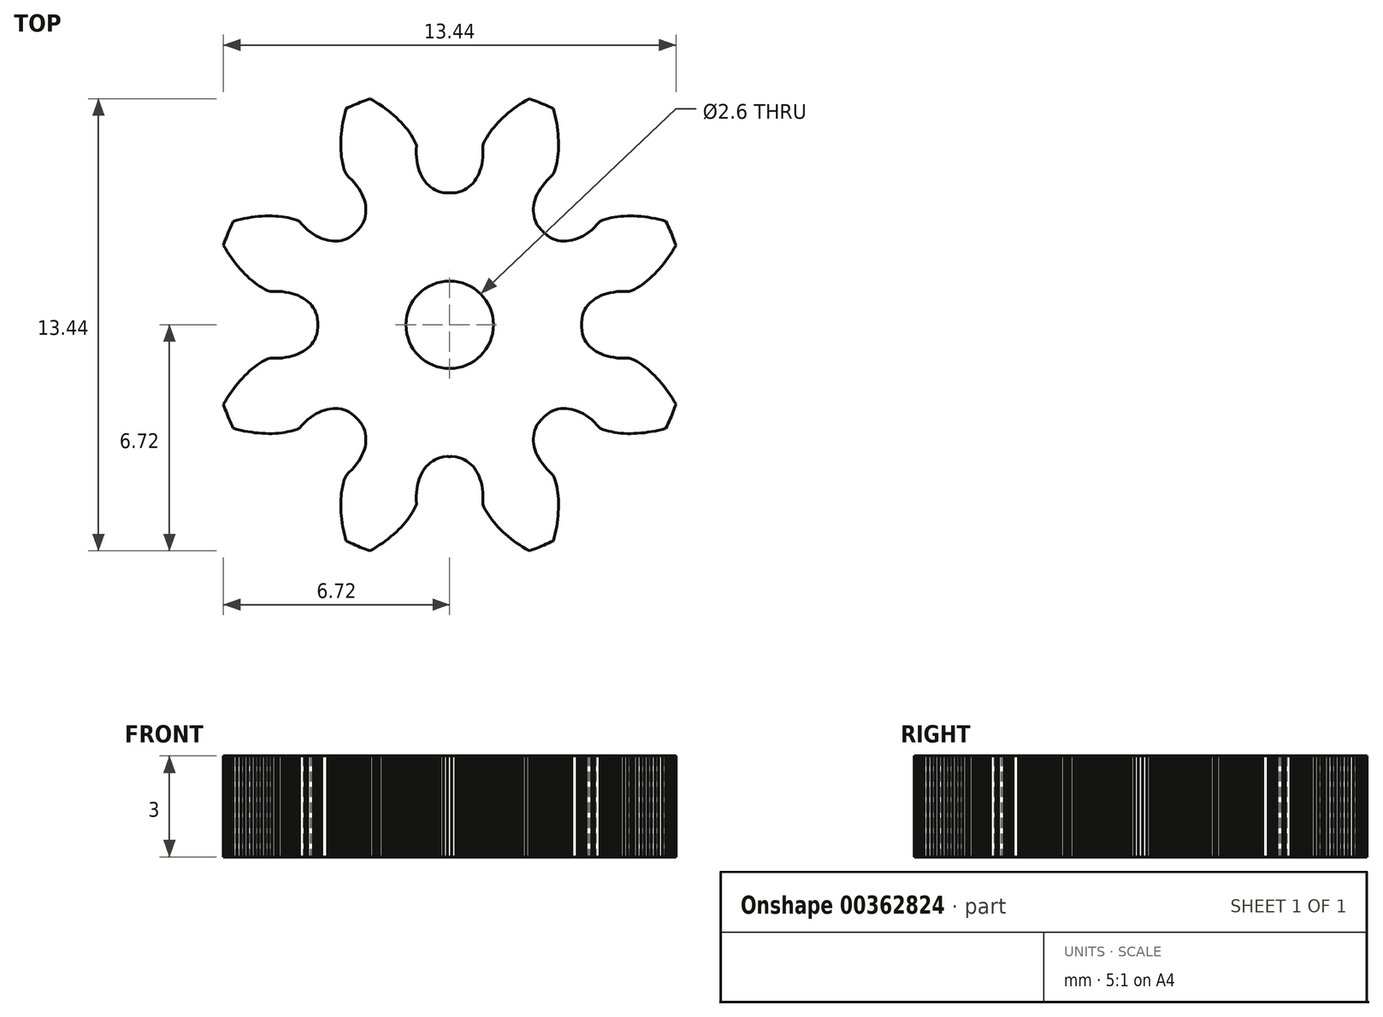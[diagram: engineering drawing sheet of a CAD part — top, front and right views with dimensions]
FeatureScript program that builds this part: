
annotation { "Feature Type Name" : "Feature", "Feature Type Description" : "" }
export const myFeature = defineFeature(function(context is Context, id is Id, definition is map)
    precondition{}
    {
        {
            var Q0;
            Q0=qCreatedBy(makeId("Top.planeOp"),FACE);
            var sketch = newSketch(context, id + "F0", { "sketchPlane" : qUnion([Q0])});
            skLineSegment(sketch, "E0", {"start": v(3.92, 0) * mm, "end": v(3.92, 0.01) * mm});
            skLineSegment(sketch, "E1", {"start": v(3.92, 0.01) * mm, "end": v(3.92, 0.03) * mm});
            skLineSegment(sketch, "E2", {"start": v(3.92, 0.03) * mm, "end": v(3.92, 0.04) * mm});
            skLineSegment(sketch, "E3", {"start": v(3.92, 0.04) * mm, "end": v(3.92, 0.05) * mm});
            skLineSegment(sketch, "E4", {"start": v(3.92, 0.05) * mm, "end": v(3.92, 0.06) * mm});
            skLineSegment(sketch, "E5", {"start": v(3.92, 0.06) * mm, "end": v(3.93, 0.18) * mm});
            skLineSegment(sketch, "E6", {"start": v(3.93, 0.18) * mm, "end": v(3.95, 0.28) * mm});
            skLineSegment(sketch, "E7", {"start": v(3.95, 0.28) * mm, "end": v(3.97, 0.36) * mm});
            skLineSegment(sketch, "E8", {"start": v(3.97, 0.36) * mm, "end": v(4, 0.44) * mm});
            skLineSegment(sketch, "E9", {"start": v(4, 0.44) * mm, "end": v(4.05, 0.5) * mm});
            skLineSegment(sketch, "E10", {"start": v(4.05, 0.5) * mm, "end": v(4.1, 0.57) * mm});
            skLineSegment(sketch, "E11", {"start": v(4.1, 0.57) * mm, "end": v(4.15, 0.63) * mm});
            skLineSegment(sketch, "E12", {"start": v(4.15, 0.63) * mm, "end": v(4.2, 0.69) * mm});
            skLineSegment(sketch, "E13", {"start": v(4.2, 0.69) * mm, "end": v(4.27, 0.74) * mm});
            skLineSegment(sketch, "E14", {"start": v(4.27, 0.74) * mm, "end": v(4.34, 0.79) * mm});
            skLineSegment(sketch, "E15", {"start": v(4.34, 0.79) * mm, "end": v(4.42, 0.83) * mm});
            skLineSegment(sketch, "E16", {"start": v(4.42, 0.83) * mm, "end": v(4.5, 0.87) * mm});
            skLineSegment(sketch, "E17", {"start": v(4.5, 0.87) * mm, "end": v(4.58, 0.9) * mm});
            skLineSegment(sketch, "E18", {"start": v(4.58, 0.9) * mm, "end": v(4.67, 0.93) * mm});
            skLineSegment(sketch, "E19", {"start": v(4.67, 0.93) * mm, "end": v(4.77, 0.96) * mm});
            skLineSegment(sketch, "E20", {"start": v(4.77, 0.96) * mm, "end": v(4.87, 0.97) * mm});
            skLineSegment(sketch, "E21", {"start": v(4.87, 0.97) * mm, "end": v(4.98, 0.99) * mm});
            skLineSegment(sketch, "E22", {"start": v(4.98, 0.99) * mm, "end": v(5.1, 1) * mm});
            skLineSegment(sketch, "E23", {"start": v(5.1, 1) * mm, "end": v(5.2, 0.99) * mm});
            skLineSegment(sketch, "E24", {"start": v(5.2, 0.99) * mm, "end": v(5.33, 0.99) * mm});
            skLineSegment(sketch, "E25", {"start": v(5.33, 0.99) * mm, "end": v(5.41, 1.02) * mm});
            skLineSegment(sketch, "E26", {"start": v(5.41, 1.02) * mm, "end": v(5.49, 1.06) * mm});
            skLineSegment(sketch, "E27", {"start": v(5.49, 1.06) * mm, "end": v(5.57, 1.1) * mm});
            skLineSegment(sketch, "E28", {"start": v(5.57, 1.1) * mm, "end": v(5.65, 1.15) * mm});
            skLineSegment(sketch, "E29", {"start": v(5.65, 1.15) * mm, "end": v(5.72, 1.2) * mm});
            skLineSegment(sketch, "E30", {"start": v(5.72, 1.2) * mm, "end": v(5.8, 1.25) * mm});
            skLineSegment(sketch, "E31", {"start": v(5.8, 1.25) * mm, "end": v(5.87, 1.31) * mm});
            skLineSegment(sketch, "E32", {"start": v(5.87, 1.31) * mm, "end": v(5.94, 1.38) * mm});
            skLineSegment(sketch, "E33", {"start": v(5.94, 1.38) * mm, "end": v(6.02, 1.44) * mm});
            skLineSegment(sketch, "E34", {"start": v(6.02, 1.44) * mm, "end": v(6.09, 1.51) * mm});
            skLineSegment(sketch, "E35", {"start": v(6.09, 1.51) * mm, "end": v(6.16, 1.58) * mm});
            skLineSegment(sketch, "E36", {"start": v(6.16, 1.58) * mm, "end": v(6.23, 1.66) * mm});
            skLineSegment(sketch, "E37", {"start": v(6.23, 1.66) * mm, "end": v(6.3, 1.74) * mm});
            skLineSegment(sketch, "E38", {"start": v(6.3, 1.74) * mm, "end": v(6.36, 1.82) * mm});
            skLineSegment(sketch, "E39", {"start": v(6.36, 1.82) * mm, "end": v(6.42, 1.9) * mm});
            skLineSegment(sketch, "E40", {"start": v(6.42, 1.9) * mm, "end": v(6.48, 2) * mm});
            skLineSegment(sketch, "E41", {"start": v(6.48, 2) * mm, "end": v(6.55, 2.08) * mm});
            skLineSegment(sketch, "E42", {"start": v(6.55, 2.08) * mm, "end": v(6.6, 2.17) * mm});
            skLineSegment(sketch, "E43", {"start": v(6.6, 2.17) * mm, "end": v(6.66, 2.27) * mm});
            skLineSegment(sketch, "E44", {"start": v(6.66, 2.27) * mm, "end": v(6.72, 2.37) * mm});
            skLineSegment(sketch, "E45", {"start": v(6.72, 2.37) * mm, "end": v(6.7, 2.44) * mm});
            skLineSegment(sketch, "E46", {"start": v(6.7, 2.44) * mm, "end": v(6.67, 2.51) * mm});
            skLineSegment(sketch, "E47", {"start": v(6.67, 2.51) * mm, "end": v(6.64, 2.58) * mm});
            skLineSegment(sketch, "E48", {"start": v(6.64, 2.58) * mm, "end": v(6.61, 2.66) * mm});
            skLineSegment(sketch, "E49", {"start": v(6.61, 2.66) * mm, "end": v(6.58, 2.73) * mm});
            skPoint(sketch, "E50", {"position": v(0, 5.7) * mm});
            skPoint(sketch, "E51", {"position": v(5.7, 0) * mm});
            skPoint(sketch, "E52", {"position": v(0, 0) * mm});
            skPoint(sketch, "E53", {"position": v(0, -5.7) * mm});
            skCircle(sketch, "E54", {"center": v(0, 0) * mm, "radius": 5.7 * mm, "construction": true});
            skLineSegment(sketch, "E55", {"start": v(5.7, 0) * mm, "end": v(-5.7, 0) * mm, "construction": true});
            skLineSegment(sketch, "E56", {"start": v(0, 5.7) * mm, "end": v(0, -5.7) * mm, "construction": true});
            skLineSegment(sketch, "E57.MirrorCS", {"start": v(3.92, 0) * mm, "end": v(3.92, -0.01) * mm});
            skLineSegment(sketch, "E58.MirrorCS", {"start": v(3.92, -0.03) * mm, "end": v(3.92, -0.04) * mm});
            skLineSegment(sketch, "E59.MirrorCS", {"start": v(3.92, -0.05) * mm, "end": v(3.92, -0.06) * mm});
            skLineSegment(sketch, "E60.MirrorCS", {"start": v(3.92, -0.01) * mm, "end": v(3.92, -0.03) * mm});
            skLineSegment(sketch, "E61.MirrorCS", {"start": v(3.92, -0.04) * mm, "end": v(3.92, -0.05) * mm});
            skLineSegment(sketch, "E62.MirrorCS", {"start": v(6.09, -1.51) * mm, "end": v(6.16, -1.58) * mm});
            skLineSegment(sketch, "E63.MirrorCS", {"start": v(4.67, -0.93) * mm, "end": v(4.77, -0.96) * mm});
            skLineSegment(sketch, "E64.MirrorCS", {"start": v(4.2, -0.69) * mm, "end": v(4.27, -0.74) * mm});
            skLineSegment(sketch, "E65.MirrorCS", {"start": v(4.27, -0.74) * mm, "end": v(4.34, -0.79) * mm});
            skLineSegment(sketch, "E66.MirrorCS", {"start": v(4.34, -0.79) * mm, "end": v(4.42, -0.83) * mm});
            skLineSegment(sketch, "E67.MirrorCS", {"start": v(3.92, -0.06) * mm, "end": v(3.93, -0.18) * mm});
            skLineSegment(sketch, "E68.MirrorCS", {"start": v(3.93, -0.18) * mm, "end": v(3.95, -0.28) * mm});
            skLineSegment(sketch, "E69.MirrorCS", {"start": v(3.95, -0.28) * mm, "end": v(3.97, -0.36) * mm});
            skLineSegment(sketch, "E70.MirrorCS", {"start": v(6.02, -1.44) * mm, "end": v(6.09, -1.51) * mm});
            skLineSegment(sketch, "E71.MirrorCS", {"start": v(3.97, -0.36) * mm, "end": v(4, -0.44) * mm});
            skLineSegment(sketch, "E72.MirrorCS", {"start": v(4, -0.44) * mm, "end": v(4.05, -0.5) * mm});
            skLineSegment(sketch, "E73.MirrorCS", {"start": v(4.05, -0.5) * mm, "end": v(4.1, -0.57) * mm});
            skLineSegment(sketch, "E74.MirrorCS", {"start": v(4.1, -0.57) * mm, "end": v(4.15, -0.63) * mm});
            skLineSegment(sketch, "E75.MirrorCS", {"start": v(4.15, -0.63) * mm, "end": v(4.2, -0.69) * mm});
            skLineSegment(sketch, "E76.MirrorCS", {"start": v(5.49, -1.06) * mm, "end": v(5.57, -1.1) * mm});
            skLineSegment(sketch, "E77.MirrorCS", {"start": v(6.6, -2.17) * mm, "end": v(6.66, -2.27) * mm});
            skLineSegment(sketch, "E78.MirrorCS", {"start": v(6.36, -1.82) * mm, "end": v(6.42, -1.9) * mm});
            skLineSegment(sketch, "E79.MirrorCS", {"start": v(5.1, -1) * mm, "end": v(5.2, -0.99) * mm});
            skLineSegment(sketch, "E80.MirrorCS", {"start": v(4.77, -0.96) * mm, "end": v(4.87, -0.97) * mm});
            skLineSegment(sketch, "E81.MirrorCS", {"start": v(6.72, -2.37) * mm, "end": v(6.7, -2.44) * mm});
            skLineSegment(sketch, "E82.MirrorCS", {"start": v(5.41, -1.02) * mm, "end": v(5.49, -1.06) * mm});
            skLineSegment(sketch, "E83.MirrorCS", {"start": v(5.65, -1.15) * mm, "end": v(5.72, -1.2) * mm});
            skLineSegment(sketch, "E84.MirrorCS", {"start": v(6.16, -1.58) * mm, "end": v(6.23, -1.66) * mm});
            skLineSegment(sketch, "E85.MirrorCS", {"start": v(4.42, -0.83) * mm, "end": v(4.5, -0.87) * mm});
            skLineSegment(sketch, "E86.MirrorCS", {"start": v(6.55, -2.08) * mm, "end": v(6.6, -2.17) * mm});
            skLineSegment(sketch, "E87.MirrorCS", {"start": v(6.64, -2.58) * mm, "end": v(6.61, -2.66) * mm});
            skLineSegment(sketch, "E88.MirrorCS", {"start": v(5.87, -1.31) * mm, "end": v(5.94, -1.38) * mm});
            skLineSegment(sketch, "E89.MirrorCS", {"start": v(6.66, -2.27) * mm, "end": v(6.72, -2.37) * mm});
            skLineSegment(sketch, "E90.MirrorCS", {"start": v(5.57, -1.1) * mm, "end": v(5.65, -1.15) * mm});
            skLineSegment(sketch, "E91.MirrorCS", {"start": v(6.42, -1.9) * mm, "end": v(6.48, -2) * mm});
            skLineSegment(sketch, "E92.MirrorCS", {"start": v(5.2, -0.99) * mm, "end": v(5.33, -0.99) * mm});
            skLineSegment(sketch, "E93.MirrorCS", {"start": v(4.87, -0.97) * mm, "end": v(4.98, -0.99) * mm});
            skLineSegment(sketch, "E94.MirrorCS", {"start": v(6.7, -2.44) * mm, "end": v(6.67, -2.51) * mm});
            skLineSegment(sketch, "E95.MirrorCS", {"start": v(5.72, -1.2) * mm, "end": v(5.8, -1.25) * mm});
            skLineSegment(sketch, "E96.MirrorCS", {"start": v(4.58, -0.9) * mm, "end": v(4.67, -0.93) * mm});
            skLineSegment(sketch, "E97.MirrorCS", {"start": v(6.23, -1.66) * mm, "end": v(6.3, -1.74) * mm});
            skLineSegment(sketch, "E98.MirrorCS", {"start": v(4.5, -0.87) * mm, "end": v(4.58, -0.9) * mm});
            skLineSegment(sketch, "E99.MirrorCS", {"start": v(6.61, -2.66) * mm, "end": v(6.58, -2.73) * mm});
            skLineSegment(sketch, "E100.MirrorCS", {"start": v(5.94, -1.38) * mm, "end": v(6.02, -1.44) * mm});
            skLineSegment(sketch, "E101.MirrorCS", {"start": v(6.48, -2) * mm, "end": v(6.55, -2.08) * mm});
            skLineSegment(sketch, "E102.MirrorCS", {"start": v(5.33, -0.99) * mm, "end": v(5.41, -1.02) * mm});
            skLineSegment(sketch, "E103.MirrorCS", {"start": v(6.67, -2.51) * mm, "end": v(6.64, -2.58) * mm});
            skLineSegment(sketch, "E104.MirrorCS", {"start": v(4.98, -0.99) * mm, "end": v(5.1, -1) * mm});
            skLineSegment(sketch, "E105.MirrorCS", {"start": v(6.3, -1.74) * mm, "end": v(6.36, -1.82) * mm});
            skLineSegment(sketch, "E106.MirrorCS", {"start": v(5.8, -1.25) * mm, "end": v(5.87, -1.31) * mm});
            skPoint(sketch, "E107.1.0", {"position": v(4.03, 4.03) * mm});
            skPoint(sketch, "E107.1.1", {"position": v(4.03, 4.03) * mm});
            skLineSegment(sketch, "E107.1.2", {"start": v(4.22, 2.82) * mm, "end": v(4.3, 2.9) * mm});
            skLineSegment(sketch, "E107.1.3", {"start": v(5.58, 3.23) * mm, "end": v(5.68, 3.22) * mm});
            skLineSegment(sketch, "E107.1.4", {"start": v(5.37, 3.23) * mm, "end": v(5.47, 3.23) * mm});
            skLineSegment(sketch, "E107.1.5", {"start": v(3.16, 6.1) * mm, "end": v(3.13, 6.2) * mm});
            skLineSegment(sketch, "E107.1.6", {"start": v(3.1, 4.54) * mm, "end": v(3.14, 4.63) * mm});
            skLineSegment(sketch, "E107.1.7", {"start": v(5.78, 3.2) * mm, "end": v(5.89, 3.2) * mm});
            skLineSegment(sketch, "E107.1.8", {"start": v(2.65, 3.96) * mm, "end": v(2.7, 4.05) * mm});
            skLineSegment(sketch, "E107.1.9", {"start": v(3.06, 2.56) * mm, "end": v(3.15, 2.52) * mm});
            skLineSegment(sketch, "E107.1.10", {"start": v(4.8, 3.18) * mm, "end": v(4.9, 3.2) * mm});
            skLineSegment(sketch, "E107.1.11", {"start": v(3.23, 5.37) * mm, "end": v(3.23, 5.47) * mm});
            skLineSegment(sketch, "E107.1.12", {"start": v(3.1, 6.32) * mm, "end": v(3.08, 6.43) * mm});
            skLineSegment(sketch, "E107.1.13", {"start": v(3.46, 2.49) * mm, "end": v(3.54, 2.5) * mm});
            skLineSegment(sketch, "E107.1.14", {"start": v(3.16, 4.71) * mm, "end": v(3.18, 4.8) * mm});
            skLineSegment(sketch, "E107.1.15", {"start": v(4.05, 2.7) * mm, "end": v(4.13, 2.76) * mm});
            skLineSegment(sketch, "E107.1.16", {"start": v(3.88, 2.6) * mm, "end": v(3.96, 2.65) * mm});
            skLineSegment(sketch, "E107.1.17", {"start": v(4.54, 3.1) * mm, "end": v(4.63, 3.14) * mm});
            skLineSegment(sketch, "E107.1.18", {"start": v(3.63, 2.51) * mm, "end": v(3.71, 2.54) * mm});
            skLineSegment(sketch, "E107.1.19", {"start": v(6.32, 3.1) * mm, "end": v(6.43, 3.08) * mm});
            skLineSegment(sketch, "E107.1.20", {"start": v(3.22, 2.5) * mm, "end": v(3.3, 2.5) * mm});
            skLineSegment(sketch, "E107.1.21", {"start": v(3.23, 5.58) * mm, "end": v(3.22, 5.68) * mm});
            skLineSegment(sketch, "E107.1.22", {"start": v(3.2, 4.9) * mm, "end": v(3.21, 4.99) * mm});
            skLineSegment(sketch, "E107.1.23", {"start": v(4.71, 3.16) * mm, "end": v(4.8, 3.18) * mm});
            skLineSegment(sketch, "E107.1.24", {"start": v(3.96, 2.65) * mm, "end": v(4.05, 2.7) * mm});
            skLineSegment(sketch, "E107.1.25", {"start": v(3.13, 6.2) * mm, "end": v(3.1, 6.32) * mm});
            skLineSegment(sketch, "E107.1.26", {"start": v(4.9, 3.2) * mm, "end": v(4.99, 3.21) * mm});
            skLineSegment(sketch, "E107.1.27", {"start": v(3.14, 4.63) * mm, "end": v(3.16, 4.71) * mm});
            skLineSegment(sketch, "E107.1.28", {"start": v(2.7, 4.05) * mm, "end": v(2.76, 4.13) * mm});
            skLineSegment(sketch, "E107.1.29", {"start": v(4.3, 2.9) * mm, "end": v(4.38, 2.98) * mm});
            skLineSegment(sketch, "E107.1.30", {"start": v(5.08, 3.22) * mm, "end": v(5.18, 3.23) * mm});
            skLineSegment(sketch, "E107.1.31", {"start": v(5.68, 3.22) * mm, "end": v(5.78, 3.2) * mm});
            skLineSegment(sketch, "E107.1.32", {"start": v(3.8, 2.57) * mm, "end": v(3.88, 2.6) * mm});
            skLineSegment(sketch, "E107.1.33", {"start": v(3.15, 2.52) * mm, "end": v(3.22, 2.5) * mm});
            skLineSegment(sketch, "E107.1.34", {"start": v(3.54, 2.5) * mm, "end": v(3.63, 2.51) * mm});
            skLineSegment(sketch, "E107.1.35", {"start": v(3.23, 5.47) * mm, "end": v(3.23, 5.58) * mm});
            skLineSegment(sketch, "E107.1.36", {"start": v(3.18, 4.8) * mm, "end": v(3.2, 4.9) * mm});
            skLineSegment(sketch, "E107.1.37", {"start": v(3.3, 2.5) * mm, "end": v(3.38, 2.49) * mm});
            skLineSegment(sketch, "E107.1.38", {"start": v(3.22, 5.68) * mm, "end": v(3.2, 5.78) * mm});
            skLineSegment(sketch, "E107.1.39", {"start": v(3.21, 4.99) * mm, "end": v(3.22, 5.08) * mm});
            skLineSegment(sketch, "E107.1.40", {"start": v(4.99, 3.21) * mm, "end": v(5.08, 3.22) * mm});
            skLineSegment(sketch, "E107.1.41", {"start": v(6.55, 2.8) * mm, "end": v(6.58, 2.73) * mm});
            skLineSegment(sketch, "E107.1.42", {"start": v(2.49, 3.46) * mm, "end": v(2.5, 3.54) * mm});
            skLineSegment(sketch, "E107.1.43", {"start": v(2.5, 3.54) * mm, "end": v(2.51, 3.63) * mm});
            skLineSegment(sketch, "E107.1.44", {"start": v(2.51, 3.63) * mm, "end": v(2.54, 3.71) * mm});
            skLineSegment(sketch, "E107.1.45", {"start": v(2.65, 2.9) * mm, "end": v(2.6, 2.99) * mm});
            skLineSegment(sketch, "E107.1.46", {"start": v(2.6, 2.99) * mm, "end": v(2.56, 3.06) * mm});
            skLineSegment(sketch, "E107.1.47", {"start": v(2.56, 3.06) * mm, "end": v(2.52, 3.15) * mm});
            skLineSegment(sketch, "E107.1.48", {"start": v(2.52, 3.15) * mm, "end": v(2.5, 3.22) * mm});
            skLineSegment(sketch, "E107.1.49", {"start": v(2.5, 3.22) * mm, "end": v(2.5, 3.3) * mm});
            skLineSegment(sketch, "E107.1.50", {"start": v(2.5, 3.3) * mm, "end": v(2.49, 3.38) * mm});
            skLineSegment(sketch, "E107.1.51", {"start": v(2.49, 3.38) * mm, "end": v(2.49, 3.46) * mm});
            skLineSegment(sketch, "E107.1.52", {"start": v(5.18, 3.23) * mm, "end": v(5.27, 3.23) * mm});
            skLineSegment(sketch, "E107.1.53", {"start": v(3.2, 5.78) * mm, "end": v(3.2, 5.89) * mm});
            skLineSegment(sketch, "E107.1.54", {"start": v(5.89, 3.2) * mm, "end": v(6, 3.18) * mm});
            skLineSegment(sketch, "E107.1.55", {"start": v(3.38, 2.49) * mm, "end": v(3.46, 2.49) * mm});
            skLineSegment(sketch, "E107.1.56", {"start": v(2.54, 3.71) * mm, "end": v(2.57, 3.8) * mm});
            skLineSegment(sketch, "E107.1.57", {"start": v(5.47, 3.23) * mm, "end": v(5.58, 3.23) * mm});
            skLineSegment(sketch, "E107.1.58", {"start": v(3.22, 5.08) * mm, "end": v(3.23, 5.18) * mm});
            skLineSegment(sketch, "E107.1.59", {"start": v(3.2, 5.89) * mm, "end": v(3.18, 6) * mm});
            skLineSegment(sketch, "E107.1.60", {"start": v(2.98, 4.38) * mm, "end": v(3.07, 4.47) * mm});
            skLineSegment(sketch, "E107.1.61", {"start": v(4.38, 2.98) * mm, "end": v(4.47, 3.07) * mm});
            skLineSegment(sketch, "E107.1.62", {"start": v(4.63, 3.14) * mm, "end": v(4.71, 3.16) * mm});
            skLineSegment(sketch, "E107.1.63", {"start": v(2.57, 3.8) * mm, "end": v(2.6, 3.88) * mm});
            skLineSegment(sketch, "E107.1.64", {"start": v(3.71, 2.54) * mm, "end": v(3.8, 2.57) * mm});
            skLineSegment(sketch, "E107.1.65", {"start": v(3.23, 5.18) * mm, "end": v(3.23, 5.27) * mm});
            skLineSegment(sketch, "E107.1.66", {"start": v(6, 3.18) * mm, "end": v(6.1, 3.16) * mm});
            skLineSegment(sketch, "E107.1.67", {"start": v(3.18, 6) * mm, "end": v(3.16, 6.1) * mm});
            skLineSegment(sketch, "E107.1.68", {"start": v(3.07, 4.47) * mm, "end": v(3.1, 4.54) * mm});
            skLineSegment(sketch, "E107.1.69", {"start": v(4.13, 2.76) * mm, "end": v(4.22, 2.82) * mm});
            skLineSegment(sketch, "E107.1.70", {"start": v(6.2, 3.13) * mm, "end": v(6.32, 3.1) * mm});
            skLineSegment(sketch, "E107.1.71", {"start": v(2.6, 3.88) * mm, "end": v(2.65, 3.96) * mm});
            skLineSegment(sketch, "E107.1.72", {"start": v(6.1, 3.16) * mm, "end": v(6.2, 3.13) * mm});
            skLineSegment(sketch, "E107.1.73", {"start": v(5.27, 3.23) * mm, "end": v(5.37, 3.23) * mm});
            skLineSegment(sketch, "E107.1.74", {"start": v(3.23, 5.27) * mm, "end": v(3.23, 5.37) * mm});
            skLineSegment(sketch, "E107.1.75", {"start": v(4.47, 3.07) * mm, "end": v(4.54, 3.1) * mm});
            skLineSegment(sketch, "E107.1.76", {"start": v(2.76, 4.13) * mm, "end": v(2.82, 4.22) * mm});
            skLineSegment(sketch, "E107.1.77", {"start": v(2.82, 4.22) * mm, "end": v(2.9, 4.3) * mm});
            skLineSegment(sketch, "E107.1.78", {"start": v(2.9, 4.3) * mm, "end": v(2.98, 4.38) * mm});
            skLineSegment(sketch, "E107.1.79", {"start": v(2.8, 6.55) * mm, "end": v(2.73, 6.58) * mm});
            skLineSegment(sketch, "E107.1.80", {"start": v(6.46, 3) * mm, "end": v(6.5, 2.94) * mm});
            skLineSegment(sketch, "E107.1.81", {"start": v(6.52, 2.87) * mm, "end": v(6.55, 2.8) * mm});
            skLineSegment(sketch, "E107.1.82", {"start": v(6.5, 2.94) * mm, "end": v(6.52, 2.87) * mm});
            skLineSegment(sketch, "E107.1.83", {"start": v(3, 6.46) * mm, "end": v(2.94, 6.5) * mm});
            skLineSegment(sketch, "E107.1.84", {"start": v(6.43, 3.08) * mm, "end": v(6.46, 3) * mm});
            skLineSegment(sketch, "E107.1.85", {"start": v(3.08, 6.43) * mm, "end": v(3, 6.46) * mm});
            skLineSegment(sketch, "E107.1.86", {"start": v(2.94, 6.5) * mm, "end": v(2.87, 6.52) * mm});
            skLineSegment(sketch, "E107.1.87", {"start": v(2.9, 2.65) * mm, "end": v(2.99, 2.6) * mm});
            skLineSegment(sketch, "E107.1.88", {"start": v(2.87, 6.52) * mm, "end": v(2.8, 6.55) * mm});
            skLineSegment(sketch, "E107.1.89", {"start": v(2.99, 2.6) * mm, "end": v(3.06, 2.56) * mm});
            skLineSegment(sketch, "E107.1.90", {"start": v(2.82, 2.73) * mm, "end": v(2.9, 2.65) * mm});
            skLineSegment(sketch, "E107.1.91", {"start": v(2.79, 2.75) * mm, "end": v(2.8, 2.74) * mm});
            skLineSegment(sketch, "E107.1.92", {"start": v(2.76, 2.78) * mm, "end": v(2.75, 2.79) * mm});
            skLineSegment(sketch, "E107.1.93", {"start": v(2.73, 2.82) * mm, "end": v(2.65, 2.9) * mm});
            skLineSegment(sketch, "E107.1.94", {"start": v(2.74, 2.8) * mm, "end": v(2.73, 2.82) * mm});
            skLineSegment(sketch, "E107.1.95", {"start": v(2.74, 2.8) * mm, "end": v(2.74, 2.8) * mm});
            skLineSegment(sketch, "E107.1.96", {"start": v(2.75, 2.79) * mm, "end": v(2.74, 2.8) * mm});
            skLineSegment(sketch, "E107.1.97", {"start": v(2.77, 2.77) * mm, "end": v(2.76, 2.78) * mm});
            skLineSegment(sketch, "E107.1.98", {"start": v(2.77, 2.77) * mm, "end": v(2.78, 2.76) * mm});
            skLineSegment(sketch, "E107.1.99", {"start": v(2.78, 2.76) * mm, "end": v(2.79, 2.75) * mm});
            skLineSegment(sketch, "E107.1.100", {"start": v(2.8, 2.74) * mm, "end": v(2.8, 2.74) * mm});
            skLineSegment(sketch, "E107.1.101", {"start": v(2.8, 2.74) * mm, "end": v(2.82, 2.73) * mm});
            skLineSegment(sketch, "E107.2.2", {"start": v(0.99, 4.98) * mm, "end": v(1, 5.1) * mm});
            skLineSegment(sketch, "E107.2.3", {"start": v(1.66, 6.23) * mm, "end": v(1.74, 6.3) * mm});
            skLineSegment(sketch, "E107.2.4", {"start": v(1.51, 6.09) * mm, "end": v(1.58, 6.16) * mm});
            skLineSegment(sketch, "E107.2.5", {"start": v(-2.08, 6.55) * mm, "end": v(-2.17, 6.6) * mm});
            skLineSegment(sketch, "E107.2.6", {"start": v(-1.02, 5.41) * mm, "end": v(-1.06, 5.49) * mm});
            skLineSegment(sketch, "E107.2.7", {"start": v(1.82, 6.36) * mm, "end": v(1.9, 6.42) * mm});
            skLineSegment(sketch, "E107.2.8", {"start": v(-0.93, 4.67) * mm, "end": v(-0.96, 4.77) * mm});
            skLineSegment(sketch, "E107.2.9", {"start": v(0.36, 3.97) * mm, "end": v(0.44, 4) * mm});
            skLineSegment(sketch, "E107.2.10", {"start": v(1.15, 5.65) * mm, "end": v(1.2, 5.72) * mm});
            skLineSegment(sketch, "E107.2.11", {"start": v(-1.51, 6.09) * mm, "end": v(-1.58, 6.16) * mm});
            skLineSegment(sketch, "E107.2.12", {"start": v(-2.27, 6.66) * mm, "end": v(-2.37, 6.72) * mm});
            skLineSegment(sketch, "E107.2.13", {"start": v(0.69, 4.2) * mm, "end": v(0.74, 4.27) * mm});
            skLineSegment(sketch, "E107.2.14", {"start": v(-1.1, 5.57) * mm, "end": v(-1.15, 5.65) * mm});
            skLineSegment(sketch, "E107.2.15", {"start": v(0.96, 4.77) * mm, "end": v(0.97, 4.87) * mm});
            skLineSegment(sketch, "E107.2.16", {"start": v(0.9, 4.58) * mm, "end": v(0.93, 4.67) * mm});
            skLineSegment(sketch, "E107.2.17", {"start": v(1.02, 5.41) * mm, "end": v(1.06, 5.49) * mm});
            skLineSegment(sketch, "E107.2.18", {"start": v(0.79, 4.34) * mm, "end": v(0.83, 4.42) * mm});
            skLineSegment(sketch, "E107.2.19", {"start": v(2.27, 6.66) * mm, "end": v(2.37, 6.72) * mm});
            skLineSegment(sketch, "E107.2.20", {"start": v(0.5, 4.05) * mm, "end": v(0.57, 4.1) * mm});
            skLineSegment(sketch, "E107.2.21", {"start": v(-1.66, 6.23) * mm, "end": v(-1.74, 6.3) * mm});
            skLineSegment(sketch, "E107.2.22", {"start": v(-1.2, 5.72) * mm, "end": v(-1.25, 5.8) * mm});
            skLineSegment(sketch, "E107.2.23", {"start": v(1.1, 5.57) * mm, "end": v(1.15, 5.65) * mm});
            skLineSegment(sketch, "E107.2.24", {"start": v(0.93, 4.67) * mm, "end": v(0.96, 4.77) * mm});
            skLineSegment(sketch, "E107.2.25", {"start": v(-2.17, 6.6) * mm, "end": v(-2.27, 6.66) * mm});
            skLineSegment(sketch, "E107.2.26", {"start": v(1.2, 5.72) * mm, "end": v(1.25, 5.8) * mm});
            skLineSegment(sketch, "E107.2.27", {"start": v(-1.06, 5.49) * mm, "end": v(-1.1, 5.57) * mm});
            skLineSegment(sketch, "E107.2.28", {"start": v(-0.96, 4.77) * mm, "end": v(-0.97, 4.87) * mm});
            skLineSegment(sketch, "E107.2.29", {"start": v(1, 5.1) * mm, "end": v(0.99, 5.2) * mm});
            skLineSegment(sketch, "E107.2.30", {"start": v(1.31, 5.87) * mm, "end": v(1.38, 5.94) * mm});
            skLineSegment(sketch, "E107.2.31", {"start": v(1.74, 6.3) * mm, "end": v(1.82, 6.36) * mm});
            skLineSegment(sketch, "E107.2.32", {"start": v(0.87, 4.5) * mm, "end": v(0.9, 4.58) * mm});
            skLineSegment(sketch, "E107.2.33", {"start": v(0.44, 4) * mm, "end": v(0.5, 4.05) * mm});
            skLineSegment(sketch, "E107.2.34", {"start": v(0.74, 4.27) * mm, "end": v(0.79, 4.34) * mm});
            skLineSegment(sketch, "E107.2.35", {"start": v(-1.58, 6.16) * mm, "end": v(-1.66, 6.23) * mm});
            skLineSegment(sketch, "E107.2.36", {"start": v(-1.15, 5.65) * mm, "end": v(-1.2, 5.72) * mm});
            skLineSegment(sketch, "E107.2.37", {"start": v(0.57, 4.1) * mm, "end": v(0.63, 4.15) * mm});
            skLineSegment(sketch, "E107.2.38", {"start": v(-1.74, 6.3) * mm, "end": v(-1.82, 6.36) * mm});
            skLineSegment(sketch, "E107.2.39", {"start": v(-1.25, 5.8) * mm, "end": v(-1.31, 5.87) * mm});
            skLineSegment(sketch, "E107.2.40", {"start": v(1.25, 5.8) * mm, "end": v(1.31, 5.87) * mm});
            skLineSegment(sketch, "E107.2.41", {"start": v(2.66, 6.61) * mm, "end": v(2.73, 6.58) * mm});
            skLineSegment(sketch, "E107.2.42", {"start": v(-0.69, 4.2) * mm, "end": v(-0.74, 4.27) * mm});
            skLineSegment(sketch, "E107.2.43", {"start": v(-0.74, 4.27) * mm, "end": v(-0.79, 4.34) * mm});
            skLineSegment(sketch, "E107.2.44", {"start": v(-0.79, 4.34) * mm, "end": v(-0.83, 4.42) * mm});
            skLineSegment(sketch, "E107.2.45", {"start": v(-0.18, 3.93) * mm, "end": v(-0.28, 3.95) * mm});
            skLineSegment(sketch, "E107.2.46", {"start": v(-0.28, 3.95) * mm, "end": v(-0.36, 3.97) * mm});
            skLineSegment(sketch, "E107.2.47", {"start": v(-0.36, 3.97) * mm, "end": v(-0.44, 4) * mm});
            skLineSegment(sketch, "E107.2.48", {"start": v(-0.44, 4) * mm, "end": v(-0.5, 4.05) * mm});
            skLineSegment(sketch, "E107.2.49", {"start": v(-0.5, 4.05) * mm, "end": v(-0.57, 4.1) * mm});
            skLineSegment(sketch, "E107.2.50", {"start": v(-0.57, 4.1) * mm, "end": v(-0.63, 4.15) * mm});
            skLineSegment(sketch, "E107.2.51", {"start": v(-0.63, 4.15) * mm, "end": v(-0.69, 4.2) * mm});
            skLineSegment(sketch, "E107.2.52", {"start": v(1.38, 5.94) * mm, "end": v(1.44, 6.02) * mm});
            skLineSegment(sketch, "E107.2.53", {"start": v(-1.82, 6.36) * mm, "end": v(-1.9, 6.42) * mm});
            skLineSegment(sketch, "E107.2.54", {"start": v(1.9, 6.42) * mm, "end": v(2, 6.48) * mm});
            skLineSegment(sketch, "E107.2.55", {"start": v(0.63, 4.15) * mm, "end": v(0.69, 4.2) * mm});
            skLineSegment(sketch, "E107.2.56", {"start": v(-0.83, 4.42) * mm, "end": v(-0.87, 4.5) * mm});
            skLineSegment(sketch, "E107.2.57", {"start": v(1.58, 6.16) * mm, "end": v(1.66, 6.23) * mm});
            skLineSegment(sketch, "E107.2.58", {"start": v(-1.31, 5.87) * mm, "end": v(-1.38, 5.94) * mm});
            skLineSegment(sketch, "E107.2.59", {"start": v(-1.9, 6.42) * mm, "end": v(-2, 6.48) * mm});
            skLineSegment(sketch, "E107.2.60", {"start": v(-0.99, 5.2) * mm, "end": v(-0.99, 5.33) * mm});
            skLineSegment(sketch, "E107.2.61", {"start": v(0.99, 5.2) * mm, "end": v(0.99, 5.33) * mm});
            skLineSegment(sketch, "E107.2.62", {"start": v(1.06, 5.49) * mm, "end": v(1.1, 5.57) * mm});
            skLineSegment(sketch, "E107.2.63", {"start": v(-0.87, 4.5) * mm, "end": v(-0.9, 4.58) * mm});
            skLineSegment(sketch, "E107.2.64", {"start": v(0.83, 4.42) * mm, "end": v(0.87, 4.5) * mm});
            skLineSegment(sketch, "E107.2.65", {"start": v(-1.38, 5.94) * mm, "end": v(-1.44, 6.02) * mm});
            skLineSegment(sketch, "E107.2.66", {"start": v(2, 6.48) * mm, "end": v(2.08, 6.55) * mm});
            skLineSegment(sketch, "E107.2.67", {"start": v(-2, 6.48) * mm, "end": v(-2.08, 6.55) * mm});
            skLineSegment(sketch, "E107.2.68", {"start": v(-0.99, 5.33) * mm, "end": v(-1.02, 5.41) * mm});
            skLineSegment(sketch, "E107.2.69", {"start": v(0.97, 4.87) * mm, "end": v(0.99, 4.98) * mm});
            skLineSegment(sketch, "E107.2.70", {"start": v(2.17, 6.6) * mm, "end": v(2.27, 6.66) * mm});
            skLineSegment(sketch, "E107.2.71", {"start": v(-0.9, 4.58) * mm, "end": v(-0.93, 4.67) * mm});
            skLineSegment(sketch, "E107.2.72", {"start": v(2.08, 6.55) * mm, "end": v(2.17, 6.6) * mm});
            skLineSegment(sketch, "E107.2.73", {"start": v(1.44, 6.02) * mm, "end": v(1.51, 6.09) * mm});
            skLineSegment(sketch, "E107.2.74", {"start": v(-1.44, 6.02) * mm, "end": v(-1.51, 6.09) * mm});
            skLineSegment(sketch, "E107.2.75", {"start": v(0.99, 5.33) * mm, "end": v(1.02, 5.41) * mm});
            skLineSegment(sketch, "E107.2.76", {"start": v(-0.97, 4.87) * mm, "end": v(-0.99, 4.98) * mm});
            skLineSegment(sketch, "E107.2.77", {"start": v(-0.99, 4.98) * mm, "end": v(-1, 5.1) * mm});
            skLineSegment(sketch, "E107.2.78", {"start": v(-1, 5.1) * mm, "end": v(-0.99, 5.2) * mm});
            skLineSegment(sketch, "E107.2.79", {"start": v(-2.66, 6.61) * mm, "end": v(-2.73, 6.58) * mm});
            skLineSegment(sketch, "E107.2.80", {"start": v(2.44, 6.7) * mm, "end": v(2.51, 6.67) * mm});
            skLineSegment(sketch, "E107.2.81", {"start": v(2.58, 6.64) * mm, "end": v(2.66, 6.61) * mm});
            skLineSegment(sketch, "E107.2.82", {"start": v(2.51, 6.67) * mm, "end": v(2.58, 6.64) * mm});
            skLineSegment(sketch, "E107.2.83", {"start": v(-2.44, 6.7) * mm, "end": v(-2.51, 6.67) * mm});
            skLineSegment(sketch, "E107.2.84", {"start": v(2.37, 6.72) * mm, "end": v(2.44, 6.7) * mm});
            skLineSegment(sketch, "E107.2.85", {"start": v(-2.37, 6.72) * mm, "end": v(-2.44, 6.7) * mm});
            skLineSegment(sketch, "E107.2.86", {"start": v(-2.51, 6.67) * mm, "end": v(-2.58, 6.64) * mm});
            skLineSegment(sketch, "E107.2.87", {"start": v(0.18, 3.93) * mm, "end": v(0.28, 3.95) * mm});
            skLineSegment(sketch, "E107.2.88", {"start": v(-2.58, 6.64) * mm, "end": v(-2.66, 6.61) * mm});
            skLineSegment(sketch, "E107.2.89", {"start": v(0.28, 3.95) * mm, "end": v(0.36, 3.97) * mm});
            skLineSegment(sketch, "E107.2.90", {"start": v(0.06, 3.92) * mm, "end": v(0.18, 3.93) * mm});
            skLineSegment(sketch, "E107.2.91", {"start": v(0.03, 3.92) * mm, "end": v(0.04, 3.92) * mm});
            skLineSegment(sketch, "E107.2.92", {"start": v(-0.01, 3.92) * mm, "end": v(-0.03, 3.92) * mm});
            skLineSegment(sketch, "E107.2.93", {"start": v(-0.06, 3.92) * mm, "end": v(-0.18, 3.93) * mm});
            skLineSegment(sketch, "E107.2.94", {"start": v(-0.05, 3.92) * mm, "end": v(-0.06, 3.92) * mm});
            skLineSegment(sketch, "E107.2.95", {"start": v(-0.04, 3.92) * mm, "end": v(-0.05, 3.92) * mm});
            skLineSegment(sketch, "E107.2.96", {"start": v(-0.03, 3.92) * mm, "end": v(-0.04, 3.92) * mm});
            skLineSegment(sketch, "E107.2.97", {"start": v(0, 3.92) * mm, "end": v(-0.01, 3.92) * mm});
            skLineSegment(sketch, "E107.2.98", {"start": v(0, 3.92) * mm, "end": v(0.01, 3.92) * mm});
            skLineSegment(sketch, "E107.2.99", {"start": v(0.01, 3.92) * mm, "end": v(0.03, 3.92) * mm});
            skLineSegment(sketch, "E107.2.100", {"start": v(0.04, 3.92) * mm, "end": v(0.05, 3.92) * mm});
            skLineSegment(sketch, "E107.2.101", {"start": v(0.05, 3.92) * mm, "end": v(0.06, 3.92) * mm});
            skPoint(sketch, "E107.3.0", {"position": v(-4.03, 4.03) * mm});
            skPoint(sketch, "E107.3.1", {"position": v(-4.03, 4.03) * mm});
            skLineSegment(sketch, "E107.3.2", {"start": v(-2.82, 4.22) * mm, "end": v(-2.9, 4.3) * mm});
            skLineSegment(sketch, "E107.3.3", {"start": v(-3.23, 5.58) * mm, "end": v(-3.22, 5.68) * mm});
            skLineSegment(sketch, "E107.3.4", {"start": v(-3.23, 5.37) * mm, "end": v(-3.23, 5.47) * mm});
            skLineSegment(sketch, "E107.3.5", {"start": v(-6.1, 3.16) * mm, "end": v(-6.2, 3.13) * mm});
            skLineSegment(sketch, "E107.3.6", {"start": v(-4.54, 3.1) * mm, "end": v(-4.63, 3.14) * mm});
            skLineSegment(sketch, "E107.3.7", {"start": v(-3.2, 5.78) * mm, "end": v(-3.2, 5.89) * mm});
            skLineSegment(sketch, "E107.3.8", {"start": v(-3.96, 2.65) * mm, "end": v(-4.05, 2.7) * mm});
            skLineSegment(sketch, "E107.3.9", {"start": v(-2.56, 3.06) * mm, "end": v(-2.52, 3.15) * mm});
            skLineSegment(sketch, "E107.3.10", {"start": v(-3.18, 4.8) * mm, "end": v(-3.2, 4.9) * mm});
            skLineSegment(sketch, "E107.3.11", {"start": v(-5.37, 3.23) * mm, "end": v(-5.47, 3.23) * mm});
            skLineSegment(sketch, "E107.3.12", {"start": v(-6.32, 3.1) * mm, "end": v(-6.43, 3.08) * mm});
            skLineSegment(sketch, "E107.3.13", {"start": v(-2.49, 3.46) * mm, "end": v(-2.5, 3.54) * mm});
            skLineSegment(sketch, "E107.3.14", {"start": v(-4.71, 3.16) * mm, "end": v(-4.8, 3.18) * mm});
            skLineSegment(sketch, "E107.3.15", {"start": v(-2.7, 4.05) * mm, "end": v(-2.76, 4.13) * mm});
            skLineSegment(sketch, "E107.3.16", {"start": v(-2.6, 3.88) * mm, "end": v(-2.65, 3.96) * mm});
            skLineSegment(sketch, "E107.3.17", {"start": v(-3.1, 4.54) * mm, "end": v(-3.14, 4.63) * mm});
            skLineSegment(sketch, "E107.3.18", {"start": v(-2.51, 3.63) * mm, "end": v(-2.54, 3.71) * mm});
            skLineSegment(sketch, "E107.3.19", {"start": v(-3.1, 6.32) * mm, "end": v(-3.08, 6.43) * mm});
            skLineSegment(sketch, "E107.3.20", {"start": v(-2.5, 3.22) * mm, "end": v(-2.5, 3.3) * mm});
            skLineSegment(sketch, "E107.3.21", {"start": v(-5.58, 3.23) * mm, "end": v(-5.68, 3.22) * mm});
            skLineSegment(sketch, "E107.3.22", {"start": v(-4.9, 3.2) * mm, "end": v(-4.99, 3.21) * mm});
            skLineSegment(sketch, "E107.3.23", {"start": v(-3.16, 4.71) * mm, "end": v(-3.18, 4.8) * mm});
            skLineSegment(sketch, "E107.3.24", {"start": v(-2.65, 3.96) * mm, "end": v(-2.7, 4.05) * mm});
            skLineSegment(sketch, "E107.3.25", {"start": v(-6.2, 3.13) * mm, "end": v(-6.32, 3.1) * mm});
            skLineSegment(sketch, "E107.3.26", {"start": v(-3.2, 4.9) * mm, "end": v(-3.21, 4.99) * mm});
            skLineSegment(sketch, "E107.3.27", {"start": v(-4.63, 3.14) * mm, "end": v(-4.71, 3.16) * mm});
            skLineSegment(sketch, "E107.3.28", {"start": v(-4.05, 2.7) * mm, "end": v(-4.13, 2.76) * mm});
            skLineSegment(sketch, "E107.3.29", {"start": v(-2.9, 4.3) * mm, "end": v(-2.98, 4.38) * mm});
            skLineSegment(sketch, "E107.3.30", {"start": v(-3.22, 5.08) * mm, "end": v(-3.23, 5.18) * mm});
            skLineSegment(sketch, "E107.3.31", {"start": v(-3.22, 5.68) * mm, "end": v(-3.2, 5.78) * mm});
            skLineSegment(sketch, "E107.3.32", {"start": v(-2.57, 3.8) * mm, "end": v(-2.6, 3.88) * mm});
            skLineSegment(sketch, "E107.3.33", {"start": v(-2.52, 3.15) * mm, "end": v(-2.5, 3.22) * mm});
            skLineSegment(sketch, "E107.3.34", {"start": v(-2.5, 3.54) * mm, "end": v(-2.51, 3.63) * mm});
            skLineSegment(sketch, "E107.3.35", {"start": v(-5.47, 3.23) * mm, "end": v(-5.58, 3.23) * mm});
            skLineSegment(sketch, "E107.3.36", {"start": v(-4.8, 3.18) * mm, "end": v(-4.9, 3.2) * mm});
            skLineSegment(sketch, "E107.3.37", {"start": v(-2.5, 3.3) * mm, "end": v(-2.49, 3.38) * mm});
            skLineSegment(sketch, "E107.3.38", {"start": v(-5.68, 3.22) * mm, "end": v(-5.78, 3.2) * mm});
            skLineSegment(sketch, "E107.3.39", {"start": v(-4.99, 3.21) * mm, "end": v(-5.08, 3.22) * mm});
            skLineSegment(sketch, "E107.3.40", {"start": v(-3.21, 4.99) * mm, "end": v(-3.22, 5.08) * mm});
            skLineSegment(sketch, "E107.3.41", {"start": v(-2.8, 6.55) * mm, "end": v(-2.73, 6.58) * mm});
            skLineSegment(sketch, "E107.3.42", {"start": v(-3.46, 2.49) * mm, "end": v(-3.54, 2.5) * mm});
            skLineSegment(sketch, "E107.3.43", {"start": v(-3.54, 2.5) * mm, "end": v(-3.63, 2.51) * mm});
            skLineSegment(sketch, "E107.3.44", {"start": v(-3.63, 2.51) * mm, "end": v(-3.71, 2.54) * mm});
            skLineSegment(sketch, "E107.3.45", {"start": v(-2.9, 2.65) * mm, "end": v(-2.99, 2.6) * mm});
            skLineSegment(sketch, "E107.3.46", {"start": v(-2.99, 2.6) * mm, "end": v(-3.06, 2.56) * mm});
            skLineSegment(sketch, "E107.3.47", {"start": v(-3.06, 2.56) * mm, "end": v(-3.15, 2.52) * mm});
            skLineSegment(sketch, "E107.3.48", {"start": v(-3.15, 2.52) * mm, "end": v(-3.22, 2.5) * mm});
            skLineSegment(sketch, "E107.3.49", {"start": v(-3.22, 2.5) * mm, "end": v(-3.3, 2.5) * mm});
            skLineSegment(sketch, "E107.3.50", {"start": v(-3.3, 2.5) * mm, "end": v(-3.38, 2.49) * mm});
            skLineSegment(sketch, "E107.3.51", {"start": v(-3.38, 2.49) * mm, "end": v(-3.46, 2.49) * mm});
            skLineSegment(sketch, "E107.3.52", {"start": v(-3.23, 5.18) * mm, "end": v(-3.23, 5.27) * mm});
            skLineSegment(sketch, "E107.3.53", {"start": v(-5.78, 3.2) * mm, "end": v(-5.89, 3.2) * mm});
            skLineSegment(sketch, "E107.3.54", {"start": v(-3.2, 5.89) * mm, "end": v(-3.18, 6) * mm});
            skLineSegment(sketch, "E107.3.55", {"start": v(-2.49, 3.38) * mm, "end": v(-2.49, 3.46) * mm});
            skLineSegment(sketch, "E107.3.56", {"start": v(-3.71, 2.54) * mm, "end": v(-3.8, 2.57) * mm});
            skLineSegment(sketch, "E107.3.57", {"start": v(-3.23, 5.47) * mm, "end": v(-3.23, 5.58) * mm});
            skLineSegment(sketch, "E107.3.58", {"start": v(-5.08, 3.22) * mm, "end": v(-5.18, 3.23) * mm});
            skLineSegment(sketch, "E107.3.59", {"start": v(-5.89, 3.2) * mm, "end": v(-6, 3.18) * mm});
            skLineSegment(sketch, "E107.3.60", {"start": v(-4.38, 2.98) * mm, "end": v(-4.47, 3.07) * mm});
            skLineSegment(sketch, "E107.3.61", {"start": v(-2.98, 4.38) * mm, "end": v(-3.07, 4.47) * mm});
            skLineSegment(sketch, "E107.3.62", {"start": v(-3.14, 4.63) * mm, "end": v(-3.16, 4.71) * mm});
            skLineSegment(sketch, "E107.3.63", {"start": v(-3.8, 2.57) * mm, "end": v(-3.88, 2.6) * mm});
            skLineSegment(sketch, "E107.3.64", {"start": v(-2.54, 3.71) * mm, "end": v(-2.57, 3.8) * mm});
            skLineSegment(sketch, "E107.3.65", {"start": v(-5.18, 3.23) * mm, "end": v(-5.27, 3.23) * mm});
            skLineSegment(sketch, "E107.3.66", {"start": v(-3.18, 6) * mm, "end": v(-3.16, 6.1) * mm});
            skLineSegment(sketch, "E107.3.67", {"start": v(-6, 3.18) * mm, "end": v(-6.1, 3.16) * mm});
            skLineSegment(sketch, "E107.3.68", {"start": v(-4.47, 3.07) * mm, "end": v(-4.54, 3.1) * mm});
            skLineSegment(sketch, "E107.3.69", {"start": v(-2.76, 4.13) * mm, "end": v(-2.82, 4.22) * mm});
            skLineSegment(sketch, "E107.3.70", {"start": v(-3.13, 6.2) * mm, "end": v(-3.1, 6.32) * mm});
            skLineSegment(sketch, "E107.3.71", {"start": v(-3.88, 2.6) * mm, "end": v(-3.96, 2.65) * mm});
            skLineSegment(sketch, "E107.3.72", {"start": v(-3.16, 6.1) * mm, "end": v(-3.13, 6.2) * mm});
            skLineSegment(sketch, "E107.3.73", {"start": v(-3.23, 5.27) * mm, "end": v(-3.23, 5.37) * mm});
            skLineSegment(sketch, "E107.3.74", {"start": v(-5.27, 3.23) * mm, "end": v(-5.37, 3.23) * mm});
            skLineSegment(sketch, "E107.3.75", {"start": v(-3.07, 4.47) * mm, "end": v(-3.1, 4.54) * mm});
            skLineSegment(sketch, "E107.3.76", {"start": v(-4.13, 2.76) * mm, "end": v(-4.22, 2.82) * mm});
            skLineSegment(sketch, "E107.3.77", {"start": v(-4.22, 2.82) * mm, "end": v(-4.3, 2.9) * mm});
            skLineSegment(sketch, "E107.3.78", {"start": v(-4.3, 2.9) * mm, "end": v(-4.38, 2.98) * mm});
            skLineSegment(sketch, "E107.3.79", {"start": v(-6.55, 2.8) * mm, "end": v(-6.58, 2.73) * mm});
            skLineSegment(sketch, "E107.3.80", {"start": v(-3, 6.46) * mm, "end": v(-2.94, 6.5) * mm});
            skLineSegment(sketch, "E107.3.81", {"start": v(-2.87, 6.52) * mm, "end": v(-2.8, 6.55) * mm});
            skLineSegment(sketch, "E107.3.82", {"start": v(-2.94, 6.5) * mm, "end": v(-2.87, 6.52) * mm});
            skLineSegment(sketch, "E107.3.83", {"start": v(-6.46, 3) * mm, "end": v(-6.5, 2.94) * mm});
            skLineSegment(sketch, "E107.3.84", {"start": v(-3.08, 6.43) * mm, "end": v(-3, 6.46) * mm});
            skLineSegment(sketch, "E107.3.85", {"start": v(-6.43, 3.08) * mm, "end": v(-6.46, 3) * mm});
            skLineSegment(sketch, "E107.3.86", {"start": v(-6.5, 2.94) * mm, "end": v(-6.52, 2.87) * mm});
            skLineSegment(sketch, "E107.3.87", {"start": v(-2.65, 2.9) * mm, "end": v(-2.6, 2.99) * mm});
            skLineSegment(sketch, "E107.3.88", {"start": v(-6.52, 2.87) * mm, "end": v(-6.55, 2.8) * mm});
            skLineSegment(sketch, "E107.3.89", {"start": v(-2.6, 2.99) * mm, "end": v(-2.56, 3.06) * mm});
            skLineSegment(sketch, "E107.3.90", {"start": v(-2.73, 2.82) * mm, "end": v(-2.65, 2.9) * mm});
            skLineSegment(sketch, "E107.3.91", {"start": v(-2.75, 2.79) * mm, "end": v(-2.74, 2.8) * mm});
            skLineSegment(sketch, "E107.3.92", {"start": v(-2.78, 2.76) * mm, "end": v(-2.79, 2.75) * mm});
            skLineSegment(sketch, "E107.3.93", {"start": v(-2.82, 2.73) * mm, "end": v(-2.9, 2.65) * mm});
            skLineSegment(sketch, "E107.3.94", {"start": v(-2.8, 2.74) * mm, "end": v(-2.82, 2.73) * mm});
            skLineSegment(sketch, "E107.3.95", {"start": v(-2.8, 2.74) * mm, "end": v(-2.8, 2.74) * mm});
            skLineSegment(sketch, "E107.3.96", {"start": v(-2.79, 2.75) * mm, "end": v(-2.8, 2.74) * mm});
            skLineSegment(sketch, "E107.3.97", {"start": v(-2.77, 2.77) * mm, "end": v(-2.78, 2.76) * mm});
            skLineSegment(sketch, "E107.3.98", {"start": v(-2.77, 2.77) * mm, "end": v(-2.76, 2.78) * mm});
            skLineSegment(sketch, "E107.3.99", {"start": v(-2.76, 2.78) * mm, "end": v(-2.75, 2.79) * mm});
            skLineSegment(sketch, "E107.3.100", {"start": v(-2.74, 2.8) * mm, "end": v(-2.74, 2.8) * mm});
            skLineSegment(sketch, "E107.3.101", {"start": v(-2.74, 2.8) * mm, "end": v(-2.73, 2.82) * mm});
            skPoint(sketch, "E107.4.0", {"position": v(-5.7, 0) * mm});
            skPoint(sketch, "E107.4.1", {"position": v(-5.7, 0) * mm});
            skLineSegment(sketch, "E107.4.2", {"start": v(-4.98, 0.99) * mm, "end": v(-5.1, 1) * mm});
            skLineSegment(sketch, "E107.4.3", {"start": v(-6.23, 1.66) * mm, "end": v(-6.3, 1.74) * mm});
            skLineSegment(sketch, "E107.4.4", {"start": v(-6.09, 1.51) * mm, "end": v(-6.16, 1.58) * mm});
            skLineSegment(sketch, "E107.4.5", {"start": v(-6.55, -2.08) * mm, "end": v(-6.6, -2.17) * mm});
            skLineSegment(sketch, "E107.4.6", {"start": v(-5.41, -1.02) * mm, "end": v(-5.49, -1.06) * mm});
            skLineSegment(sketch, "E107.4.7", {"start": v(-6.36, 1.82) * mm, "end": v(-6.42, 1.9) * mm});
            skLineSegment(sketch, "E107.4.8", {"start": v(-4.67, -0.93) * mm, "end": v(-4.77, -0.96) * mm});
            skLineSegment(sketch, "E107.4.9", {"start": v(-3.97, 0.36) * mm, "end": v(-4, 0.44) * mm});
            skLineSegment(sketch, "E107.4.10", {"start": v(-5.65, 1.15) * mm, "end": v(-5.72, 1.2) * mm});
            skLineSegment(sketch, "E107.4.11", {"start": v(-6.09, -1.51) * mm, "end": v(-6.16, -1.58) * mm});
            skLineSegment(sketch, "E107.4.12", {"start": v(-6.66, -2.27) * mm, "end": v(-6.72, -2.37) * mm});
            skLineSegment(sketch, "E107.4.13", {"start": v(-4.2, 0.69) * mm, "end": v(-4.27, 0.74) * mm});
            skLineSegment(sketch, "E107.4.14", {"start": v(-5.57, -1.1) * mm, "end": v(-5.65, -1.15) * mm});
            skLineSegment(sketch, "E107.4.15", {"start": v(-4.77, 0.96) * mm, "end": v(-4.87, 0.97) * mm});
            skLineSegment(sketch, "E107.4.16", {"start": v(-4.58, 0.9) * mm, "end": v(-4.67, 0.93) * mm});
            skLineSegment(sketch, "E107.4.17", {"start": v(-5.41, 1.02) * mm, "end": v(-5.49, 1.06) * mm});
            skLineSegment(sketch, "E107.4.18", {"start": v(-4.34, 0.79) * mm, "end": v(-4.42, 0.83) * mm});
            skLineSegment(sketch, "E107.4.19", {"start": v(-6.66, 2.27) * mm, "end": v(-6.72, 2.37) * mm});
            skLineSegment(sketch, "E107.4.20", {"start": v(-4.05, 0.5) * mm, "end": v(-4.1, 0.57) * mm});
            skLineSegment(sketch, "E107.4.21", {"start": v(-6.23, -1.66) * mm, "end": v(-6.3, -1.74) * mm});
            skLineSegment(sketch, "E107.4.22", {"start": v(-5.72, -1.2) * mm, "end": v(-5.8, -1.25) * mm});
            skLineSegment(sketch, "E107.4.23", {"start": v(-5.57, 1.1) * mm, "end": v(-5.65, 1.15) * mm});
            skLineSegment(sketch, "E107.4.24", {"start": v(-4.67, 0.93) * mm, "end": v(-4.77, 0.96) * mm});
            skLineSegment(sketch, "E107.4.25", {"start": v(-6.6, -2.17) * mm, "end": v(-6.66, -2.27) * mm});
            skLineSegment(sketch, "E107.4.26", {"start": v(-5.72, 1.2) * mm, "end": v(-5.8, 1.25) * mm});
            skLineSegment(sketch, "E107.4.27", {"start": v(-5.49, -1.06) * mm, "end": v(-5.57, -1.1) * mm});
            skLineSegment(sketch, "E107.4.28", {"start": v(-4.77, -0.96) * mm, "end": v(-4.87, -0.97) * mm});
            skLineSegment(sketch, "E107.4.29", {"start": v(-5.1, 1) * mm, "end": v(-5.2, 0.99) * mm});
            skLineSegment(sketch, "E107.4.30", {"start": v(-5.87, 1.31) * mm, "end": v(-5.94, 1.38) * mm});
            skLineSegment(sketch, "E107.4.31", {"start": v(-6.3, 1.74) * mm, "end": v(-6.36, 1.82) * mm});
            skLineSegment(sketch, "E107.4.32", {"start": v(-4.5, 0.87) * mm, "end": v(-4.58, 0.9) * mm});
            skLineSegment(sketch, "E107.4.33", {"start": v(-4, 0.44) * mm, "end": v(-4.05, 0.5) * mm});
            skLineSegment(sketch, "E107.4.34", {"start": v(-4.27, 0.74) * mm, "end": v(-4.34, 0.79) * mm});
            skLineSegment(sketch, "E107.4.35", {"start": v(-6.16, -1.58) * mm, "end": v(-6.23, -1.66) * mm});
            skLineSegment(sketch, "E107.4.36", {"start": v(-5.65, -1.15) * mm, "end": v(-5.72, -1.2) * mm});
            skLineSegment(sketch, "E107.4.37", {"start": v(-4.1, 0.57) * mm, "end": v(-4.15, 0.63) * mm});
            skLineSegment(sketch, "E107.4.38", {"start": v(-6.3, -1.74) * mm, "end": v(-6.36, -1.82) * mm});
            skLineSegment(sketch, "E107.4.39", {"start": v(-5.8, -1.25) * mm, "end": v(-5.87, -1.31) * mm});
            skLineSegment(sketch, "E107.4.40", {"start": v(-5.8, 1.25) * mm, "end": v(-5.87, 1.31) * mm});
            skLineSegment(sketch, "E107.4.41", {"start": v(-6.61, 2.66) * mm, "end": v(-6.58, 2.73) * mm});
            skLineSegment(sketch, "E107.4.42", {"start": v(-4.2, -0.69) * mm, "end": v(-4.27, -0.74) * mm});
            skLineSegment(sketch, "E107.4.43", {"start": v(-4.27, -0.74) * mm, "end": v(-4.34, -0.79) * mm});
            skLineSegment(sketch, "E107.4.44", {"start": v(-4.34, -0.79) * mm, "end": v(-4.42, -0.83) * mm});
            skLineSegment(sketch, "E107.4.45", {"start": v(-3.93, -0.18) * mm, "end": v(-3.95, -0.28) * mm});
            skLineSegment(sketch, "E107.4.46", {"start": v(-3.95, -0.28) * mm, "end": v(-3.97, -0.36) * mm});
            skLineSegment(sketch, "E107.4.47", {"start": v(-3.97, -0.36) * mm, "end": v(-4, -0.44) * mm});
            skLineSegment(sketch, "E107.4.48", {"start": v(-4, -0.44) * mm, "end": v(-4.05, -0.5) * mm});
            skLineSegment(sketch, "E107.4.49", {"start": v(-4.05, -0.5) * mm, "end": v(-4.1, -0.57) * mm});
            skLineSegment(sketch, "E107.4.50", {"start": v(-4.1, -0.57) * mm, "end": v(-4.15, -0.63) * mm});
            skLineSegment(sketch, "E107.4.51", {"start": v(-4.15, -0.63) * mm, "end": v(-4.2, -0.69) * mm});
            skLineSegment(sketch, "E107.4.52", {"start": v(-5.94, 1.38) * mm, "end": v(-6.02, 1.44) * mm});
            skLineSegment(sketch, "E107.4.53", {"start": v(-6.36, -1.82) * mm, "end": v(-6.42, -1.9) * mm});
            skLineSegment(sketch, "E107.4.54", {"start": v(-6.42, 1.9) * mm, "end": v(-6.48, 2) * mm});
            skLineSegment(sketch, "E107.4.55", {"start": v(-4.15, 0.63) * mm, "end": v(-4.2, 0.69) * mm});
            skLineSegment(sketch, "E107.4.56", {"start": v(-4.42, -0.83) * mm, "end": v(-4.5, -0.87) * mm});
            skLineSegment(sketch, "E107.4.57", {"start": v(-6.16, 1.58) * mm, "end": v(-6.23, 1.66) * mm});
            skLineSegment(sketch, "E107.4.58", {"start": v(-5.87, -1.31) * mm, "end": v(-5.94, -1.38) * mm});
            skLineSegment(sketch, "E107.4.59", {"start": v(-6.42, -1.9) * mm, "end": v(-6.48, -2) * mm});
            skLineSegment(sketch, "E107.4.60", {"start": v(-5.2, -0.99) * mm, "end": v(-5.33, -0.99) * mm});
            skLineSegment(sketch, "E107.4.61", {"start": v(-5.2, 0.99) * mm, "end": v(-5.33, 0.99) * mm});
            skLineSegment(sketch, "E107.4.62", {"start": v(-5.49, 1.06) * mm, "end": v(-5.57, 1.1) * mm});
            skLineSegment(sketch, "E107.4.63", {"start": v(-4.5, -0.87) * mm, "end": v(-4.58, -0.9) * mm});
            skLineSegment(sketch, "E107.4.64", {"start": v(-4.42, 0.83) * mm, "end": v(-4.5, 0.87) * mm});
            skLineSegment(sketch, "E107.4.65", {"start": v(-5.94, -1.38) * mm, "end": v(-6.02, -1.44) * mm});
            skLineSegment(sketch, "E107.4.66", {"start": v(-6.48, 2) * mm, "end": v(-6.55, 2.08) * mm});
            skLineSegment(sketch, "E107.4.67", {"start": v(-6.48, -2) * mm, "end": v(-6.55, -2.08) * mm});
            skLineSegment(sketch, "E107.4.68", {"start": v(-5.33, -0.99) * mm, "end": v(-5.41, -1.02) * mm});
            skLineSegment(sketch, "E107.4.69", {"start": v(-4.87, 0.97) * mm, "end": v(-4.98, 0.99) * mm});
            skLineSegment(sketch, "E107.4.70", {"start": v(-6.6, 2.17) * mm, "end": v(-6.66, 2.27) * mm});
            skLineSegment(sketch, "E107.4.71", {"start": v(-4.58, -0.9) * mm, "end": v(-4.67, -0.93) * mm});
            skLineSegment(sketch, "E107.4.72", {"start": v(-6.55, 2.08) * mm, "end": v(-6.6, 2.17) * mm});
            skLineSegment(sketch, "E107.4.73", {"start": v(-6.02, 1.44) * mm, "end": v(-6.09, 1.51) * mm});
            skLineSegment(sketch, "E107.4.74", {"start": v(-6.02, -1.44) * mm, "end": v(-6.09, -1.51) * mm});
            skLineSegment(sketch, "E107.4.75", {"start": v(-5.33, 0.99) * mm, "end": v(-5.41, 1.02) * mm});
            skLineSegment(sketch, "E107.4.76", {"start": v(-4.87, -0.97) * mm, "end": v(-4.98, -0.99) * mm});
            skLineSegment(sketch, "E107.4.77", {"start": v(-4.98, -0.99) * mm, "end": v(-5.1, -1) * mm});
            skLineSegment(sketch, "E107.4.78", {"start": v(-5.1, -1) * mm, "end": v(-5.2, -0.99) * mm});
            skLineSegment(sketch, "E107.4.79", {"start": v(-6.61, -2.66) * mm, "end": v(-6.58, -2.73) * mm});
            skLineSegment(sketch, "E107.4.80", {"start": v(-6.7, 2.44) * mm, "end": v(-6.67, 2.51) * mm});
            skLineSegment(sketch, "E107.4.81", {"start": v(-6.64, 2.58) * mm, "end": v(-6.61, 2.66) * mm});
            skLineSegment(sketch, "E107.4.82", {"start": v(-6.67, 2.51) * mm, "end": v(-6.64, 2.58) * mm});
            skLineSegment(sketch, "E107.4.83", {"start": v(-6.7, -2.44) * mm, "end": v(-6.67, -2.51) * mm});
            skLineSegment(sketch, "E107.4.84", {"start": v(-6.72, 2.37) * mm, "end": v(-6.7, 2.44) * mm});
            skLineSegment(sketch, "E107.4.85", {"start": v(-6.72, -2.37) * mm, "end": v(-6.7, -2.44) * mm});
            skLineSegment(sketch, "E107.4.86", {"start": v(-6.67, -2.51) * mm, "end": v(-6.64, -2.58) * mm});
            skLineSegment(sketch, "E107.4.87", {"start": v(-3.93, 0.18) * mm, "end": v(-3.95, 0.28) * mm});
            skLineSegment(sketch, "E107.4.88", {"start": v(-6.64, -2.58) * mm, "end": v(-6.61, -2.66) * mm});
            skLineSegment(sketch, "E107.4.89", {"start": v(-3.95, 0.28) * mm, "end": v(-3.97, 0.36) * mm});
            skLineSegment(sketch, "E107.4.90", {"start": v(-3.92, 0.06) * mm, "end": v(-3.93, 0.18) * mm});
            skLineSegment(sketch, "E107.4.91", {"start": v(-3.92, 0.03) * mm, "end": v(-3.92, 0.04) * mm});
            skLineSegment(sketch, "E107.4.92", {"start": v(-3.92, -0.01) * mm, "end": v(-3.92, -0.03) * mm});
            skLineSegment(sketch, "E107.4.93", {"start": v(-3.92, -0.06) * mm, "end": v(-3.93, -0.18) * mm});
            skLineSegment(sketch, "E107.4.94", {"start": v(-3.92, -0.05) * mm, "end": v(-3.92, -0.06) * mm});
            skLineSegment(sketch, "E107.4.95", {"start": v(-3.92, -0.04) * mm, "end": v(-3.92, -0.05) * mm});
            skLineSegment(sketch, "E107.4.96", {"start": v(-3.92, -0.03) * mm, "end": v(-3.92, -0.04) * mm});
            skLineSegment(sketch, "E107.4.97", {"start": v(-3.92, 0) * mm, "end": v(-3.92, -0.01) * mm});
            skLineSegment(sketch, "E107.4.98", {"start": v(-3.92, 0) * mm, "end": v(-3.92, 0.01) * mm});
            skLineSegment(sketch, "E107.4.99", {"start": v(-3.92, 0.01) * mm, "end": v(-3.92, 0.03) * mm});
            skLineSegment(sketch, "E107.4.100", {"start": v(-3.92, 0.04) * mm, "end": v(-3.92, 0.05) * mm});
            skLineSegment(sketch, "E107.4.101", {"start": v(-3.92, 0.05) * mm, "end": v(-3.92, 0.06) * mm});
            skPoint(sketch, "E107.5.0", {"position": v(-4.03, -4.03) * mm});
            skPoint(sketch, "E107.5.1", {"position": v(-4.03, -4.03) * mm});
            skLineSegment(sketch, "E107.5.2", {"start": v(-4.22, -2.82) * mm, "end": v(-4.3, -2.9) * mm});
            skLineSegment(sketch, "E107.5.3", {"start": v(-5.58, -3.23) * mm, "end": v(-5.68, -3.22) * mm});
            skLineSegment(sketch, "E107.5.4", {"start": v(-5.37, -3.23) * mm, "end": v(-5.47, -3.23) * mm});
            skLineSegment(sketch, "E107.5.5", {"start": v(-3.16, -6.1) * mm, "end": v(-3.13, -6.2) * mm});
            skLineSegment(sketch, "E107.5.6", {"start": v(-3.1, -4.54) * mm, "end": v(-3.14, -4.63) * mm});
            skLineSegment(sketch, "E107.5.7", {"start": v(-5.78, -3.2) * mm, "end": v(-5.89, -3.2) * mm});
            skLineSegment(sketch, "E107.5.8", {"start": v(-2.65, -3.96) * mm, "end": v(-2.7, -4.05) * mm});
            skLineSegment(sketch, "E107.5.9", {"start": v(-3.06, -2.56) * mm, "end": v(-3.15, -2.52) * mm});
            skLineSegment(sketch, "E107.5.10", {"start": v(-4.8, -3.18) * mm, "end": v(-4.9, -3.2) * mm});
            skLineSegment(sketch, "E107.5.11", {"start": v(-3.23, -5.37) * mm, "end": v(-3.23, -5.47) * mm});
            skLineSegment(sketch, "E107.5.12", {"start": v(-3.1, -6.32) * mm, "end": v(-3.08, -6.43) * mm});
            skLineSegment(sketch, "E107.5.13", {"start": v(-3.46, -2.49) * mm, "end": v(-3.54, -2.5) * mm});
            skLineSegment(sketch, "E107.5.14", {"start": v(-3.16, -4.71) * mm, "end": v(-3.18, -4.8) * mm});
            skLineSegment(sketch, "E107.5.15", {"start": v(-4.05, -2.7) * mm, "end": v(-4.13, -2.76) * mm});
            skLineSegment(sketch, "E107.5.16", {"start": v(-3.88, -2.6) * mm, "end": v(-3.96, -2.65) * mm});
            skLineSegment(sketch, "E107.5.17", {"start": v(-4.54, -3.1) * mm, "end": v(-4.63, -3.14) * mm});
            skLineSegment(sketch, "E107.5.18", {"start": v(-3.63, -2.51) * mm, "end": v(-3.71, -2.54) * mm});
            skLineSegment(sketch, "E107.5.19", {"start": v(-6.32, -3.1) * mm, "end": v(-6.43, -3.08) * mm});
            skLineSegment(sketch, "E107.5.20", {"start": v(-3.22, -2.5) * mm, "end": v(-3.3, -2.5) * mm});
            skLineSegment(sketch, "E107.5.21", {"start": v(-3.23, -5.58) * mm, "end": v(-3.22, -5.68) * mm});
            skLineSegment(sketch, "E107.5.22", {"start": v(-3.2, -4.9) * mm, "end": v(-3.21, -4.99) * mm});
            skLineSegment(sketch, "E107.5.23", {"start": v(-4.71, -3.16) * mm, "end": v(-4.8, -3.18) * mm});
            skLineSegment(sketch, "E107.5.24", {"start": v(-3.96, -2.65) * mm, "end": v(-4.05, -2.7) * mm});
            skLineSegment(sketch, "E107.5.25", {"start": v(-3.13, -6.2) * mm, "end": v(-3.1, -6.32) * mm});
            skLineSegment(sketch, "E107.5.26", {"start": v(-4.9, -3.2) * mm, "end": v(-4.99, -3.21) * mm});
            skLineSegment(sketch, "E107.5.27", {"start": v(-3.14, -4.63) * mm, "end": v(-3.16, -4.71) * mm});
            skLineSegment(sketch, "E107.5.28", {"start": v(-2.7, -4.05) * mm, "end": v(-2.76, -4.13) * mm});
            skLineSegment(sketch, "E107.5.29", {"start": v(-4.3, -2.9) * mm, "end": v(-4.38, -2.98) * mm});
            skLineSegment(sketch, "E107.5.30", {"start": v(-5.08, -3.22) * mm, "end": v(-5.18, -3.23) * mm});
            skLineSegment(sketch, "E107.5.31", {"start": v(-5.68, -3.22) * mm, "end": v(-5.78, -3.2) * mm});
            skLineSegment(sketch, "E107.5.32", {"start": v(-3.8, -2.57) * mm, "end": v(-3.88, -2.6) * mm});
            skLineSegment(sketch, "E107.5.33", {"start": v(-3.15, -2.52) * mm, "end": v(-3.22, -2.5) * mm});
            skLineSegment(sketch, "E107.5.34", {"start": v(-3.54, -2.5) * mm, "end": v(-3.63, -2.51) * mm});
            skLineSegment(sketch, "E107.5.35", {"start": v(-3.23, -5.47) * mm, "end": v(-3.23, -5.58) * mm});
            skLineSegment(sketch, "E107.5.36", {"start": v(-3.18, -4.8) * mm, "end": v(-3.2, -4.9) * mm});
            skLineSegment(sketch, "E107.5.37", {"start": v(-3.3, -2.5) * mm, "end": v(-3.38, -2.49) * mm});
            skLineSegment(sketch, "E107.5.38", {"start": v(-3.22, -5.68) * mm, "end": v(-3.2, -5.78) * mm});
            skLineSegment(sketch, "E107.5.39", {"start": v(-3.21, -4.99) * mm, "end": v(-3.22, -5.08) * mm});
            skLineSegment(sketch, "E107.5.40", {"start": v(-4.99, -3.21) * mm, "end": v(-5.08, -3.22) * mm});
            skLineSegment(sketch, "E107.5.41", {"start": v(-6.55, -2.8) * mm, "end": v(-6.58, -2.73) * mm});
            skLineSegment(sketch, "E107.5.42", {"start": v(-2.49, -3.46) * mm, "end": v(-2.5, -3.54) * mm});
            skLineSegment(sketch, "E107.5.43", {"start": v(-2.5, -3.54) * mm, "end": v(-2.51, -3.63) * mm});
            skLineSegment(sketch, "E107.5.44", {"start": v(-2.51, -3.63) * mm, "end": v(-2.54, -3.71) * mm});
            skLineSegment(sketch, "E107.5.45", {"start": v(-2.65, -2.9) * mm, "end": v(-2.6, -2.99) * mm});
            skLineSegment(sketch, "E107.5.46", {"start": v(-2.6, -2.99) * mm, "end": v(-2.56, -3.06) * mm});
            skLineSegment(sketch, "E107.5.47", {"start": v(-2.56, -3.06) * mm, "end": v(-2.52, -3.15) * mm});
            skLineSegment(sketch, "E107.5.48", {"start": v(-2.52, -3.15) * mm, "end": v(-2.5, -3.22) * mm});
            skLineSegment(sketch, "E107.5.49", {"start": v(-2.5, -3.22) * mm, "end": v(-2.5, -3.3) * mm});
            skLineSegment(sketch, "E107.5.50", {"start": v(-2.5, -3.3) * mm, "end": v(-2.49, -3.38) * mm});
            skLineSegment(sketch, "E107.5.51", {"start": v(-2.49, -3.38) * mm, "end": v(-2.49, -3.46) * mm});
            skLineSegment(sketch, "E107.5.52", {"start": v(-5.18, -3.23) * mm, "end": v(-5.27, -3.23) * mm});
            skLineSegment(sketch, "E107.5.53", {"start": v(-3.2, -5.78) * mm, "end": v(-3.2, -5.89) * mm});
            skLineSegment(sketch, "E107.5.54", {"start": v(-5.89, -3.2) * mm, "end": v(-6, -3.18) * mm});
            skLineSegment(sketch, "E107.5.55", {"start": v(-3.38, -2.49) * mm, "end": v(-3.46, -2.49) * mm});
            skLineSegment(sketch, "E107.5.56", {"start": v(-2.54, -3.71) * mm, "end": v(-2.57, -3.8) * mm});
            skLineSegment(sketch, "E107.5.57", {"start": v(-5.47, -3.23) * mm, "end": v(-5.58, -3.23) * mm});
            skLineSegment(sketch, "E107.5.58", {"start": v(-3.22, -5.08) * mm, "end": v(-3.23, -5.18) * mm});
            skLineSegment(sketch, "E107.5.59", {"start": v(-3.2, -5.89) * mm, "end": v(-3.18, -6) * mm});
            skLineSegment(sketch, "E107.5.60", {"start": v(-2.98, -4.38) * mm, "end": v(-3.07, -4.47) * mm});
            skLineSegment(sketch, "E107.5.61", {"start": v(-4.38, -2.98) * mm, "end": v(-4.47, -3.07) * mm});
            skLineSegment(sketch, "E107.5.62", {"start": v(-4.63, -3.14) * mm, "end": v(-4.71, -3.16) * mm});
            skLineSegment(sketch, "E107.5.63", {"start": v(-2.57, -3.8) * mm, "end": v(-2.6, -3.88) * mm});
            skLineSegment(sketch, "E107.5.64", {"start": v(-3.71, -2.54) * mm, "end": v(-3.8, -2.57) * mm});
            skLineSegment(sketch, "E107.5.65", {"start": v(-3.23, -5.18) * mm, "end": v(-3.23, -5.27) * mm});
            skLineSegment(sketch, "E107.5.66", {"start": v(-6, -3.18) * mm, "end": v(-6.1, -3.16) * mm});
            skLineSegment(sketch, "E107.5.67", {"start": v(-3.18, -6) * mm, "end": v(-3.16, -6.1) * mm});
            skLineSegment(sketch, "E107.5.68", {"start": v(-3.07, -4.47) * mm, "end": v(-3.1, -4.54) * mm});
            skLineSegment(sketch, "E107.5.69", {"start": v(-4.13, -2.76) * mm, "end": v(-4.22, -2.82) * mm});
            skLineSegment(sketch, "E107.5.70", {"start": v(-6.2, -3.13) * mm, "end": v(-6.32, -3.1) * mm});
            skLineSegment(sketch, "E107.5.71", {"start": v(-2.6, -3.88) * mm, "end": v(-2.65, -3.96) * mm});
            skLineSegment(sketch, "E107.5.72", {"start": v(-6.1, -3.16) * mm, "end": v(-6.2, -3.13) * mm});
            skLineSegment(sketch, "E107.5.73", {"start": v(-5.27, -3.23) * mm, "end": v(-5.37, -3.23) * mm});
            skLineSegment(sketch, "E107.5.74", {"start": v(-3.23, -5.27) * mm, "end": v(-3.23, -5.37) * mm});
            skLineSegment(sketch, "E107.5.75", {"start": v(-4.47, -3.07) * mm, "end": v(-4.54, -3.1) * mm});
            skLineSegment(sketch, "E107.5.76", {"start": v(-2.76, -4.13) * mm, "end": v(-2.82, -4.22) * mm});
            skLineSegment(sketch, "E107.5.77", {"start": v(-2.82, -4.22) * mm, "end": v(-2.9, -4.3) * mm});
            skLineSegment(sketch, "E107.5.78", {"start": v(-2.9, -4.3) * mm, "end": v(-2.98, -4.38) * mm});
            skLineSegment(sketch, "E107.5.79", {"start": v(-2.8, -6.55) * mm, "end": v(-2.73, -6.58) * mm});
            skLineSegment(sketch, "E107.5.80", {"start": v(-6.46, -3) * mm, "end": v(-6.5, -2.94) * mm});
            skLineSegment(sketch, "E107.5.81", {"start": v(-6.52, -2.87) * mm, "end": v(-6.55, -2.8) * mm});
            skLineSegment(sketch, "E107.5.82", {"start": v(-6.5, -2.94) * mm, "end": v(-6.52, -2.87) * mm});
            skLineSegment(sketch, "E107.5.83", {"start": v(-3, -6.46) * mm, "end": v(-2.94, -6.5) * mm});
            skLineSegment(sketch, "E107.5.84", {"start": v(-6.43, -3.08) * mm, "end": v(-6.46, -3) * mm});
            skLineSegment(sketch, "E107.5.85", {"start": v(-3.08, -6.43) * mm, "end": v(-3, -6.46) * mm});
            skLineSegment(sketch, "E107.5.86", {"start": v(-2.94, -6.5) * mm, "end": v(-2.87, -6.52) * mm});
            skLineSegment(sketch, "E107.5.87", {"start": v(-2.9, -2.65) * mm, "end": v(-2.99, -2.6) * mm});
            skLineSegment(sketch, "E107.5.88", {"start": v(-2.87, -6.52) * mm, "end": v(-2.8, -6.55) * mm});
            skLineSegment(sketch, "E107.5.89", {"start": v(-2.99, -2.6) * mm, "end": v(-3.06, -2.56) * mm});
            skLineSegment(sketch, "E107.5.90", {"start": v(-2.82, -2.73) * mm, "end": v(-2.9, -2.65) * mm});
            skLineSegment(sketch, "E107.5.91", {"start": v(-2.79, -2.75) * mm, "end": v(-2.8, -2.74) * mm});
            skLineSegment(sketch, "E107.5.92", {"start": v(-2.76, -2.78) * mm, "end": v(-2.75, -2.79) * mm});
            skLineSegment(sketch, "E107.5.93", {"start": v(-2.73, -2.82) * mm, "end": v(-2.65, -2.9) * mm});
            skLineSegment(sketch, "E107.5.94", {"start": v(-2.74, -2.8) * mm, "end": v(-2.73, -2.82) * mm});
            skLineSegment(sketch, "E107.5.95", {"start": v(-2.74, -2.8) * mm, "end": v(-2.74, -2.8) * mm});
            skLineSegment(sketch, "E107.5.96", {"start": v(-2.75, -2.79) * mm, "end": v(-2.74, -2.8) * mm});
            skLineSegment(sketch, "E107.5.97", {"start": v(-2.77, -2.77) * mm, "end": v(-2.76, -2.78) * mm});
            skLineSegment(sketch, "E107.5.98", {"start": v(-2.77, -2.77) * mm, "end": v(-2.78, -2.76) * mm});
            skLineSegment(sketch, "E107.5.99", {"start": v(-2.78, -2.76) * mm, "end": v(-2.79, -2.75) * mm});
            skLineSegment(sketch, "E107.5.100", {"start": v(-2.8, -2.74) * mm, "end": v(-2.8, -2.74) * mm});
            skLineSegment(sketch, "E107.5.101", {"start": v(-2.8, -2.74) * mm, "end": v(-2.82, -2.73) * mm});
            skLineSegment(sketch, "E107.6.2", {"start": v(-0.99, -4.98) * mm, "end": v(-1, -5.1) * mm});
            skLineSegment(sketch, "E107.6.3", {"start": v(-1.66, -6.23) * mm, "end": v(-1.74, -6.3) * mm});
            skLineSegment(sketch, "E107.6.4", {"start": v(-1.51, -6.09) * mm, "end": v(-1.58, -6.16) * mm});
            skLineSegment(sketch, "E107.6.5", {"start": v(2.08, -6.55) * mm, "end": v(2.17, -6.6) * mm});
            skLineSegment(sketch, "E107.6.6", {"start": v(1.02, -5.41) * mm, "end": v(1.06, -5.49) * mm});
            skLineSegment(sketch, "E107.6.7", {"start": v(-1.82, -6.36) * mm, "end": v(-1.9, -6.42) * mm});
            skLineSegment(sketch, "E107.6.8", {"start": v(0.93, -4.67) * mm, "end": v(0.96, -4.77) * mm});
            skLineSegment(sketch, "E107.6.9", {"start": v(-0.36, -3.97) * mm, "end": v(-0.44, -4) * mm});
            skLineSegment(sketch, "E107.6.10", {"start": v(-1.15, -5.65) * mm, "end": v(-1.2, -5.72) * mm});
            skLineSegment(sketch, "E107.6.11", {"start": v(1.51, -6.09) * mm, "end": v(1.58, -6.16) * mm});
            skLineSegment(sketch, "E107.6.12", {"start": v(2.27, -6.66) * mm, "end": v(2.37, -6.72) * mm});
            skLineSegment(sketch, "E107.6.13", {"start": v(-0.69, -4.2) * mm, "end": v(-0.74, -4.27) * mm});
            skLineSegment(sketch, "E107.6.14", {"start": v(1.1, -5.57) * mm, "end": v(1.15, -5.65) * mm});
            skLineSegment(sketch, "E107.6.15", {"start": v(-0.96, -4.77) * mm, "end": v(-0.97, -4.87) * mm});
            skLineSegment(sketch, "E107.6.16", {"start": v(-0.9, -4.58) * mm, "end": v(-0.93, -4.67) * mm});
            skLineSegment(sketch, "E107.6.17", {"start": v(-1.02, -5.41) * mm, "end": v(-1.06, -5.49) * mm});
            skLineSegment(sketch, "E107.6.18", {"start": v(-0.79, -4.34) * mm, "end": v(-0.83, -4.42) * mm});
            skLineSegment(sketch, "E107.6.19", {"start": v(-2.27, -6.66) * mm, "end": v(-2.37, -6.72) * mm});
            skLineSegment(sketch, "E107.6.20", {"start": v(-0.5, -4.05) * mm, "end": v(-0.57, -4.1) * mm});
            skLineSegment(sketch, "E107.6.21", {"start": v(1.66, -6.23) * mm, "end": v(1.74, -6.3) * mm});
            skLineSegment(sketch, "E107.6.22", {"start": v(1.2, -5.72) * mm, "end": v(1.25, -5.8) * mm});
            skLineSegment(sketch, "E107.6.23", {"start": v(-1.1, -5.57) * mm, "end": v(-1.15, -5.65) * mm});
            skLineSegment(sketch, "E107.6.24", {"start": v(-0.93, -4.67) * mm, "end": v(-0.96, -4.77) * mm});
            skLineSegment(sketch, "E107.6.25", {"start": v(2.17, -6.6) * mm, "end": v(2.27, -6.66) * mm});
            skLineSegment(sketch, "E107.6.26", {"start": v(-1.2, -5.72) * mm, "end": v(-1.25, -5.8) * mm});
            skLineSegment(sketch, "E107.6.27", {"start": v(1.06, -5.49) * mm, "end": v(1.1, -5.57) * mm});
            skLineSegment(sketch, "E107.6.28", {"start": v(0.96, -4.77) * mm, "end": v(0.97, -4.87) * mm});
            skLineSegment(sketch, "E107.6.29", {"start": v(-1, -5.1) * mm, "end": v(-0.99, -5.2) * mm});
            skLineSegment(sketch, "E107.6.30", {"start": v(-1.31, -5.87) * mm, "end": v(-1.38, -5.94) * mm});
            skLineSegment(sketch, "E107.6.31", {"start": v(-1.74, -6.3) * mm, "end": v(-1.82, -6.36) * mm});
            skLineSegment(sketch, "E107.6.32", {"start": v(-0.87, -4.5) * mm, "end": v(-0.9, -4.58) * mm});
            skLineSegment(sketch, "E107.6.33", {"start": v(-0.44, -4) * mm, "end": v(-0.5, -4.05) * mm});
            skLineSegment(sketch, "E107.6.34", {"start": v(-0.74, -4.27) * mm, "end": v(-0.79, -4.34) * mm});
            skLineSegment(sketch, "E107.6.35", {"start": v(1.58, -6.16) * mm, "end": v(1.66, -6.23) * mm});
            skLineSegment(sketch, "E107.6.36", {"start": v(1.15, -5.65) * mm, "end": v(1.2, -5.72) * mm});
            skLineSegment(sketch, "E107.6.37", {"start": v(-0.57, -4.1) * mm, "end": v(-0.63, -4.15) * mm});
            skLineSegment(sketch, "E107.6.38", {"start": v(1.74, -6.3) * mm, "end": v(1.82, -6.36) * mm});
            skLineSegment(sketch, "E107.6.39", {"start": v(1.25, -5.8) * mm, "end": v(1.31, -5.87) * mm});
            skLineSegment(sketch, "E107.6.40", {"start": v(-1.25, -5.8) * mm, "end": v(-1.31, -5.87) * mm});
            skLineSegment(sketch, "E107.6.41", {"start": v(-2.66, -6.61) * mm, "end": v(-2.73, -6.58) * mm});
            skLineSegment(sketch, "E107.6.42", {"start": v(0.69, -4.2) * mm, "end": v(0.74, -4.27) * mm});
            skLineSegment(sketch, "E107.6.43", {"start": v(0.74, -4.27) * mm, "end": v(0.79, -4.34) * mm});
            skLineSegment(sketch, "E107.6.44", {"start": v(0.79, -4.34) * mm, "end": v(0.83, -4.42) * mm});
            skLineSegment(sketch, "E107.6.45", {"start": v(0.18, -3.93) * mm, "end": v(0.28, -3.95) * mm});
            skLineSegment(sketch, "E107.6.46", {"start": v(0.28, -3.95) * mm, "end": v(0.36, -3.97) * mm});
            skLineSegment(sketch, "E107.6.47", {"start": v(0.36, -3.97) * mm, "end": v(0.44, -4) * mm});
            skLineSegment(sketch, "E107.6.48", {"start": v(0.44, -4) * mm, "end": v(0.5, -4.05) * mm});
            skLineSegment(sketch, "E107.6.49", {"start": v(0.5, -4.05) * mm, "end": v(0.57, -4.1) * mm});
            skLineSegment(sketch, "E107.6.50", {"start": v(0.57, -4.1) * mm, "end": v(0.63, -4.15) * mm});
            skLineSegment(sketch, "E107.6.51", {"start": v(0.63, -4.15) * mm, "end": v(0.69, -4.2) * mm});
            skLineSegment(sketch, "E107.6.52", {"start": v(-1.38, -5.94) * mm, "end": v(-1.44, -6.02) * mm});
            skLineSegment(sketch, "E107.6.53", {"start": v(1.82, -6.36) * mm, "end": v(1.9, -6.42) * mm});
            skLineSegment(sketch, "E107.6.54", {"start": v(-1.9, -6.42) * mm, "end": v(-2, -6.48) * mm});
            skLineSegment(sketch, "E107.6.55", {"start": v(-0.63, -4.15) * mm, "end": v(-0.69, -4.2) * mm});
            skLineSegment(sketch, "E107.6.56", {"start": v(0.83, -4.42) * mm, "end": v(0.87, -4.5) * mm});
            skLineSegment(sketch, "E107.6.57", {"start": v(-1.58, -6.16) * mm, "end": v(-1.66, -6.23) * mm});
            skLineSegment(sketch, "E107.6.58", {"start": v(1.31, -5.87) * mm, "end": v(1.38, -5.94) * mm});
            skLineSegment(sketch, "E107.6.59", {"start": v(1.9, -6.42) * mm, "end": v(2, -6.48) * mm});
            skLineSegment(sketch, "E107.6.60", {"start": v(0.99, -5.2) * mm, "end": v(0.99, -5.33) * mm});
            skLineSegment(sketch, "E107.6.61", {"start": v(-0.99, -5.2) * mm, "end": v(-0.99, -5.33) * mm});
            skLineSegment(sketch, "E107.6.62", {"start": v(-1.06, -5.49) * mm, "end": v(-1.1, -5.57) * mm});
            skLineSegment(sketch, "E107.6.63", {"start": v(0.87, -4.5) * mm, "end": v(0.9, -4.58) * mm});
            skLineSegment(sketch, "E107.6.64", {"start": v(-0.83, -4.42) * mm, "end": v(-0.87, -4.5) * mm});
            skLineSegment(sketch, "E107.6.65", {"start": v(1.38, -5.94) * mm, "end": v(1.44, -6.02) * mm});
            skLineSegment(sketch, "E107.6.66", {"start": v(-2, -6.48) * mm, "end": v(-2.08, -6.55) * mm});
            skLineSegment(sketch, "E107.6.67", {"start": v(2, -6.48) * mm, "end": v(2.08, -6.55) * mm});
            skLineSegment(sketch, "E107.6.68", {"start": v(0.99, -5.33) * mm, "end": v(1.02, -5.41) * mm});
            skLineSegment(sketch, "E107.6.69", {"start": v(-0.97, -4.87) * mm, "end": v(-0.99, -4.98) * mm});
            skLineSegment(sketch, "E107.6.70", {"start": v(-2.17, -6.6) * mm, "end": v(-2.27, -6.66) * mm});
            skLineSegment(sketch, "E107.6.71", {"start": v(0.9, -4.58) * mm, "end": v(0.93, -4.67) * mm});
            skLineSegment(sketch, "E107.6.72", {"start": v(-2.08, -6.55) * mm, "end": v(-2.17, -6.6) * mm});
            skLineSegment(sketch, "E107.6.73", {"start": v(-1.44, -6.02) * mm, "end": v(-1.51, -6.09) * mm});
            skLineSegment(sketch, "E107.6.74", {"start": v(1.44, -6.02) * mm, "end": v(1.51, -6.09) * mm});
            skLineSegment(sketch, "E107.6.75", {"start": v(-0.99, -5.33) * mm, "end": v(-1.02, -5.41) * mm});
            skLineSegment(sketch, "E107.6.76", {"start": v(0.97, -4.87) * mm, "end": v(0.99, -4.98) * mm});
            skLineSegment(sketch, "E107.6.77", {"start": v(0.99, -4.98) * mm, "end": v(1, -5.1) * mm});
            skLineSegment(sketch, "E107.6.78", {"start": v(1, -5.1) * mm, "end": v(0.99, -5.2) * mm});
            skLineSegment(sketch, "E107.6.79", {"start": v(2.66, -6.61) * mm, "end": v(2.73, -6.58) * mm});
            skLineSegment(sketch, "E107.6.80", {"start": v(-2.44, -6.7) * mm, "end": v(-2.51, -6.67) * mm});
            skLineSegment(sketch, "E107.6.81", {"start": v(-2.58, -6.64) * mm, "end": v(-2.66, -6.61) * mm});
            skLineSegment(sketch, "E107.6.82", {"start": v(-2.51, -6.67) * mm, "end": v(-2.58, -6.64) * mm});
            skLineSegment(sketch, "E107.6.83", {"start": v(2.44, -6.7) * mm, "end": v(2.51, -6.67) * mm});
            skLineSegment(sketch, "E107.6.84", {"start": v(-2.37, -6.72) * mm, "end": v(-2.44, -6.7) * mm});
            skLineSegment(sketch, "E107.6.85", {"start": v(2.37, -6.72) * mm, "end": v(2.44, -6.7) * mm});
            skLineSegment(sketch, "E107.6.86", {"start": v(2.51, -6.67) * mm, "end": v(2.58, -6.64) * mm});
            skLineSegment(sketch, "E107.6.87", {"start": v(-0.18, -3.93) * mm, "end": v(-0.28, -3.95) * mm});
            skLineSegment(sketch, "E107.6.88", {"start": v(2.58, -6.64) * mm, "end": v(2.66, -6.61) * mm});
            skLineSegment(sketch, "E107.6.89", {"start": v(-0.28, -3.95) * mm, "end": v(-0.36, -3.97) * mm});
            skLineSegment(sketch, "E107.6.90", {"start": v(-0.06, -3.92) * mm, "end": v(-0.18, -3.93) * mm});
            skLineSegment(sketch, "E107.6.91", {"start": v(-0.03, -3.92) * mm, "end": v(-0.04, -3.92) * mm});
            skLineSegment(sketch, "E107.6.92", {"start": v(0.01, -3.92) * mm, "end": v(0.03, -3.92) * mm});
            skLineSegment(sketch, "E107.6.93", {"start": v(0.06, -3.92) * mm, "end": v(0.18, -3.93) * mm});
            skLineSegment(sketch, "E107.6.94", {"start": v(0.05, -3.92) * mm, "end": v(0.06, -3.92) * mm});
            skLineSegment(sketch, "E107.6.95", {"start": v(0.04, -3.92) * mm, "end": v(0.05, -3.92) * mm});
            skLineSegment(sketch, "E107.6.96", {"start": v(0.03, -3.92) * mm, "end": v(0.04, -3.92) * mm});
            skLineSegment(sketch, "E107.6.97", {"start": v(0, -3.92) * mm, "end": v(0.01, -3.92) * mm});
            skLineSegment(sketch, "E107.6.98", {"start": v(0, -3.92) * mm, "end": v(-0.01, -3.92) * mm});
            skLineSegment(sketch, "E107.6.99", {"start": v(-0.01, -3.92) * mm, "end": v(-0.03, -3.92) * mm});
            skLineSegment(sketch, "E107.6.100", {"start": v(-0.04, -3.92) * mm, "end": v(-0.05, -3.92) * mm});
            skLineSegment(sketch, "E107.6.101", {"start": v(-0.05, -3.92) * mm, "end": v(-0.06, -3.92) * mm});
            skPoint(sketch, "E107.7.0", {"position": v(4.03, -4.03) * mm});
            skPoint(sketch, "E107.7.1", {"position": v(4.03, -4.03) * mm});
            skLineSegment(sketch, "E107.7.2", {"start": v(2.82, -4.22) * mm, "end": v(2.9, -4.3) * mm});
            skLineSegment(sketch, "E107.7.3", {"start": v(3.23, -5.58) * mm, "end": v(3.22, -5.68) * mm});
            skLineSegment(sketch, "E107.7.4", {"start": v(3.23, -5.37) * mm, "end": v(3.23, -5.47) * mm});
            skLineSegment(sketch, "E107.7.5", {"start": v(6.1, -3.16) * mm, "end": v(6.2, -3.13) * mm});
            skLineSegment(sketch, "E107.7.6", {"start": v(4.54, -3.1) * mm, "end": v(4.63, -3.14) * mm});
            skLineSegment(sketch, "E107.7.7", {"start": v(3.2, -5.78) * mm, "end": v(3.2, -5.89) * mm});
            skLineSegment(sketch, "E107.7.8", {"start": v(3.96, -2.65) * mm, "end": v(4.05, -2.7) * mm});
            skLineSegment(sketch, "E107.7.9", {"start": v(2.56, -3.06) * mm, "end": v(2.52, -3.15) * mm});
            skLineSegment(sketch, "E107.7.10", {"start": v(3.18, -4.8) * mm, "end": v(3.2, -4.9) * mm});
            skLineSegment(sketch, "E107.7.11", {"start": v(5.37, -3.23) * mm, "end": v(5.47, -3.23) * mm});
            skLineSegment(sketch, "E107.7.12", {"start": v(6.32, -3.1) * mm, "end": v(6.43, -3.08) * mm});
            skLineSegment(sketch, "E107.7.13", {"start": v(2.49, -3.46) * mm, "end": v(2.5, -3.54) * mm});
            skLineSegment(sketch, "E107.7.14", {"start": v(4.71, -3.16) * mm, "end": v(4.8, -3.18) * mm});
            skLineSegment(sketch, "E107.7.15", {"start": v(2.7, -4.05) * mm, "end": v(2.76, -4.13) * mm});
            skLineSegment(sketch, "E107.7.16", {"start": v(2.6, -3.88) * mm, "end": v(2.65, -3.96) * mm});
            skLineSegment(sketch, "E107.7.17", {"start": v(3.1, -4.54) * mm, "end": v(3.14, -4.63) * mm});
            skLineSegment(sketch, "E107.7.18", {"start": v(2.51, -3.63) * mm, "end": v(2.54, -3.71) * mm});
            skLineSegment(sketch, "E107.7.19", {"start": v(3.1, -6.32) * mm, "end": v(3.08, -6.43) * mm});
            skLineSegment(sketch, "E107.7.20", {"start": v(2.5, -3.22) * mm, "end": v(2.5, -3.3) * mm});
            skLineSegment(sketch, "E107.7.21", {"start": v(5.58, -3.23) * mm, "end": v(5.68, -3.22) * mm});
            skLineSegment(sketch, "E107.7.22", {"start": v(4.9, -3.2) * mm, "end": v(4.99, -3.21) * mm});
            skLineSegment(sketch, "E107.7.23", {"start": v(3.16, -4.71) * mm, "end": v(3.18, -4.8) * mm});
            skLineSegment(sketch, "E107.7.24", {"start": v(2.65, -3.96) * mm, "end": v(2.7, -4.05) * mm});
            skLineSegment(sketch, "E107.7.25", {"start": v(6.2, -3.13) * mm, "end": v(6.32, -3.1) * mm});
            skLineSegment(sketch, "E107.7.26", {"start": v(3.2, -4.9) * mm, "end": v(3.21, -4.99) * mm});
            skLineSegment(sketch, "E107.7.27", {"start": v(4.63, -3.14) * mm, "end": v(4.71, -3.16) * mm});
            skLineSegment(sketch, "E107.7.28", {"start": v(4.05, -2.7) * mm, "end": v(4.13, -2.76) * mm});
            skLineSegment(sketch, "E107.7.29", {"start": v(2.9, -4.3) * mm, "end": v(2.98, -4.38) * mm});
            skLineSegment(sketch, "E107.7.30", {"start": v(3.22, -5.08) * mm, "end": v(3.23, -5.18) * mm});
            skLineSegment(sketch, "E107.7.31", {"start": v(3.22, -5.68) * mm, "end": v(3.2, -5.78) * mm});
            skLineSegment(sketch, "E107.7.32", {"start": v(2.57, -3.8) * mm, "end": v(2.6, -3.88) * mm});
            skLineSegment(sketch, "E107.7.33", {"start": v(2.52, -3.15) * mm, "end": v(2.5, -3.22) * mm});
            skLineSegment(sketch, "E107.7.34", {"start": v(2.5, -3.54) * mm, "end": v(2.51, -3.63) * mm});
            skLineSegment(sketch, "E107.7.35", {"start": v(5.47, -3.23) * mm, "end": v(5.58, -3.23) * mm});
            skLineSegment(sketch, "E107.7.36", {"start": v(4.8, -3.18) * mm, "end": v(4.9, -3.2) * mm});
            skLineSegment(sketch, "E107.7.37", {"start": v(2.5, -3.3) * mm, "end": v(2.49, -3.38) * mm});
            skLineSegment(sketch, "E107.7.38", {"start": v(5.68, -3.22) * mm, "end": v(5.78, -3.2) * mm});
            skLineSegment(sketch, "E107.7.39", {"start": v(4.99, -3.21) * mm, "end": v(5.08, -3.22) * mm});
            skLineSegment(sketch, "E107.7.40", {"start": v(3.21, -4.99) * mm, "end": v(3.22, -5.08) * mm});
            skLineSegment(sketch, "E107.7.41", {"start": v(2.8, -6.55) * mm, "end": v(2.73, -6.58) * mm});
            skLineSegment(sketch, "E107.7.42", {"start": v(3.46, -2.49) * mm, "end": v(3.54, -2.5) * mm});
            skLineSegment(sketch, "E107.7.43", {"start": v(3.54, -2.5) * mm, "end": v(3.63, -2.51) * mm});
            skLineSegment(sketch, "E107.7.44", {"start": v(3.63, -2.51) * mm, "end": v(3.71, -2.54) * mm});
            skLineSegment(sketch, "E107.7.45", {"start": v(2.9, -2.65) * mm, "end": v(2.99, -2.6) * mm});
            skLineSegment(sketch, "E107.7.46", {"start": v(2.99, -2.6) * mm, "end": v(3.06, -2.56) * mm});
            skLineSegment(sketch, "E107.7.47", {"start": v(3.06, -2.56) * mm, "end": v(3.15, -2.52) * mm});
            skLineSegment(sketch, "E107.7.48", {"start": v(3.15, -2.52) * mm, "end": v(3.22, -2.5) * mm});
            skLineSegment(sketch, "E107.7.49", {"start": v(3.22, -2.5) * mm, "end": v(3.3, -2.5) * mm});
            skLineSegment(sketch, "E107.7.50", {"start": v(3.3, -2.5) * mm, "end": v(3.38, -2.49) * mm});
            skLineSegment(sketch, "E107.7.51", {"start": v(3.38, -2.49) * mm, "end": v(3.46, -2.49) * mm});
            skLineSegment(sketch, "E107.7.52", {"start": v(3.23, -5.18) * mm, "end": v(3.23, -5.27) * mm});
            skLineSegment(sketch, "E107.7.53", {"start": v(5.78, -3.2) * mm, "end": v(5.89, -3.2) * mm});
            skLineSegment(sketch, "E107.7.54", {"start": v(3.2, -5.89) * mm, "end": v(3.18, -6) * mm});
            skLineSegment(sketch, "E107.7.55", {"start": v(2.49, -3.38) * mm, "end": v(2.49, -3.46) * mm});
            skLineSegment(sketch, "E107.7.56", {"start": v(3.71, -2.54) * mm, "end": v(3.8, -2.57) * mm});
            skLineSegment(sketch, "E107.7.57", {"start": v(3.23, -5.47) * mm, "end": v(3.23, -5.58) * mm});
            skLineSegment(sketch, "E107.7.58", {"start": v(5.08, -3.22) * mm, "end": v(5.18, -3.23) * mm});
            skLineSegment(sketch, "E107.7.59", {"start": v(5.89, -3.2) * mm, "end": v(6, -3.18) * mm});
            skLineSegment(sketch, "E107.7.60", {"start": v(4.38, -2.98) * mm, "end": v(4.47, -3.07) * mm});
            skLineSegment(sketch, "E107.7.61", {"start": v(2.98, -4.38) * mm, "end": v(3.07, -4.47) * mm});
            skLineSegment(sketch, "E107.7.62", {"start": v(3.14, -4.63) * mm, "end": v(3.16, -4.71) * mm});
            skLineSegment(sketch, "E107.7.63", {"start": v(3.8, -2.57) * mm, "end": v(3.88, -2.6) * mm});
            skLineSegment(sketch, "E107.7.64", {"start": v(2.54, -3.71) * mm, "end": v(2.57, -3.8) * mm});
            skLineSegment(sketch, "E107.7.65", {"start": v(5.18, -3.23) * mm, "end": v(5.27, -3.23) * mm});
            skLineSegment(sketch, "E107.7.66", {"start": v(3.18, -6) * mm, "end": v(3.16, -6.1) * mm});
            skLineSegment(sketch, "E107.7.67", {"start": v(6, -3.18) * mm, "end": v(6.1, -3.16) * mm});
            skLineSegment(sketch, "E107.7.68", {"start": v(4.47, -3.07) * mm, "end": v(4.54, -3.1) * mm});
            skLineSegment(sketch, "E107.7.69", {"start": v(2.76, -4.13) * mm, "end": v(2.82, -4.22) * mm});
            skLineSegment(sketch, "E107.7.70", {"start": v(3.13, -6.2) * mm, "end": v(3.1, -6.32) * mm});
            skLineSegment(sketch, "E107.7.71", {"start": v(3.88, -2.6) * mm, "end": v(3.96, -2.65) * mm});
            skLineSegment(sketch, "E107.7.72", {"start": v(3.16, -6.1) * mm, "end": v(3.13, -6.2) * mm});
            skLineSegment(sketch, "E107.7.73", {"start": v(3.23, -5.27) * mm, "end": v(3.23, -5.37) * mm});
            skLineSegment(sketch, "E107.7.74", {"start": v(5.27, -3.23) * mm, "end": v(5.37, -3.23) * mm});
            skLineSegment(sketch, "E107.7.75", {"start": v(3.07, -4.47) * mm, "end": v(3.1, -4.54) * mm});
            skLineSegment(sketch, "E107.7.76", {"start": v(4.13, -2.76) * mm, "end": v(4.22, -2.82) * mm});
            skLineSegment(sketch, "E107.7.77", {"start": v(4.22, -2.82) * mm, "end": v(4.3, -2.9) * mm});
            skLineSegment(sketch, "E107.7.78", {"start": v(4.3, -2.9) * mm, "end": v(4.38, -2.98) * mm});
            skLineSegment(sketch, "E107.7.79", {"start": v(6.55, -2.8) * mm, "end": v(6.58, -2.73) * mm});
            skLineSegment(sketch, "E107.7.80", {"start": v(3, -6.46) * mm, "end": v(2.94, -6.5) * mm});
            skLineSegment(sketch, "E107.7.81", {"start": v(2.87, -6.52) * mm, "end": v(2.8, -6.55) * mm});
            skLineSegment(sketch, "E107.7.82", {"start": v(2.94, -6.5) * mm, "end": v(2.87, -6.52) * mm});
            skLineSegment(sketch, "E107.7.83", {"start": v(6.46, -3) * mm, "end": v(6.5, -2.94) * mm});
            skLineSegment(sketch, "E107.7.84", {"start": v(3.08, -6.43) * mm, "end": v(3, -6.46) * mm});
            skLineSegment(sketch, "E107.7.85", {"start": v(6.43, -3.08) * mm, "end": v(6.46, -3) * mm});
            skLineSegment(sketch, "E107.7.86", {"start": v(6.5, -2.94) * mm, "end": v(6.52, -2.87) * mm});
            skLineSegment(sketch, "E107.7.87", {"start": v(2.65, -2.9) * mm, "end": v(2.6, -2.99) * mm});
            skLineSegment(sketch, "E107.7.88", {"start": v(6.52, -2.87) * mm, "end": v(6.55, -2.8) * mm});
            skLineSegment(sketch, "E107.7.89", {"start": v(2.6, -2.99) * mm, "end": v(2.56, -3.06) * mm});
            skLineSegment(sketch, "E107.7.90", {"start": v(2.73, -2.82) * mm, "end": v(2.65, -2.9) * mm});
            skLineSegment(sketch, "E107.7.91", {"start": v(2.75, -2.79) * mm, "end": v(2.74, -2.8) * mm});
            skLineSegment(sketch, "E107.7.92", {"start": v(2.78, -2.76) * mm, "end": v(2.79, -2.75) * mm});
            skLineSegment(sketch, "E107.7.93", {"start": v(2.82, -2.73) * mm, "end": v(2.9, -2.65) * mm});
            skLineSegment(sketch, "E107.7.94", {"start": v(2.8, -2.74) * mm, "end": v(2.82, -2.73) * mm});
            skLineSegment(sketch, "E107.7.95", {"start": v(2.8, -2.74) * mm, "end": v(2.8, -2.74) * mm});
            skLineSegment(sketch, "E107.7.96", {"start": v(2.79, -2.75) * mm, "end": v(2.8, -2.74) * mm});
            skLineSegment(sketch, "E107.7.97", {"start": v(2.77, -2.77) * mm, "end": v(2.78, -2.76) * mm});
            skLineSegment(sketch, "E107.7.98", {"start": v(2.77, -2.77) * mm, "end": v(2.76, -2.78) * mm});
            skLineSegment(sketch, "E107.7.99", {"start": v(2.76, -2.78) * mm, "end": v(2.75, -2.79) * mm});
            skLineSegment(sketch, "E107.7.100", {"start": v(2.74, -2.8) * mm, "end": v(2.74, -2.8) * mm});
            skLineSegment(sketch, "E107.7.101", {"start": v(2.74, -2.8) * mm, "end": v(2.73, -2.82) * mm});
            skCircle(sketch, "E108", {"center": v(0, 0) * mm, "radius": 1.3 * mm});
            skSolve(sketch);
        }
        {
            var Q0;
            Q0=qSketchRegion(id+"F0",true);
            extrude(context, id + "F1", {"entities" : qUnion([Q0]), "depth" : 3 * mm});
        }
    });
